# Revit family: AL_ST-STS1_приток
name_source: partatom
category: Воздухораспределители
revit_build: Autodesk Revit 2014 (Build: 20130308_1515(x64)
units: mm (PartAtom-declared; Revit-internal decimal feet)

## types (1242) — shared parameters
A = 23 мм
URL = http://inplast.ru
margins = 12 мм
Изготовитель = INPLAST-SMAY
Материал = Алюминий_RAL9016 (INPLAST)
Описание = Решетка AL-STS1 тип сетки - сетка просечно-вытяжная 4.5х9.0мм
Сетка = Сетка просечная[горизонтальная]_RAL9016 (INPLAST)

## per-type parameters (varying)
| type | Aef | C | C' | D | D' | Тип крепежа |
| AL-STS-1-100х100-АА | 0.006 м² | 100 мм | 95 мм | 100 мм | 95 мм | саморезы |
| AL-STS-1-125х100-АА | 0.008 м² | 125 мм | 120 мм | 100 мм | 95 мм | саморезы |
| AL-STS-1-125х125-АА | 0.009 м² | 125 мм | 120 мм | 125 мм | 120 мм | саморезы |
| AL-STS-1-150х100-АА | 0.009 м² | 150 мм | 145 мм | 100 мм | 95 мм | саморезы |
| AL-STS-1-150х125-АА | 0.011 м² | 150 мм | 145 мм | 125 мм | 120 мм | саморезы |
| AL-STS-1-150х150-АА | 0.014 м² | 150 мм | 145 мм | 150 мм | 145 мм | саморезы |
| AL-STS-1-200х100-АА | 0.012 м² | 200 мм | 195 мм | 100 мм | 95 мм | саморезы |
| AL-STS-1-200х125-АА | 0.015 м² | 200 мм | 195 мм | 125 мм | 120 мм | саморезы |
| AL-STS-1-200х150-АА | 0.018 м² | 200 мм | 195 мм | 150 мм | 145 мм | саморезы |
| AL-STS-1-200х200-АА | 0.024 м² | 200 мм | 195 мм | 200 мм | 195 мм | саморезы |
| AL-STS-1-225х100-АА | 0.014 м² | 225 мм | 220 мм | 100 мм | 95 мм | саморезы |
| AL-STS-1-225х125-АА | 0.017 м² | 225 мм | 220 мм | 125 мм | 120 мм | саморезы |
| AL-STS-1-225х150-АА | 0.020 м² | 225 мм | 220 мм | 150 мм | 145 мм | саморезы |
| AL-STS-1-225х200-АА | 0.027 м² | 225 мм | 220 мм | 200 мм | 195 мм | саморезы |
| AL-STS-1-225х225-АА | 0.030 м² | 225 мм | 220 мм | 225 мм | 220 мм | саморезы |
| AL-STS-1-250х100-АА | 0.015 м² | 250 мм | 245 мм | 100 мм | 95 мм | саморезы |
| AL-STS-1-250х125-АА | 0.019 м² | 250 мм | 245 мм | 125 мм | 120 мм | саморезы |
| AL-STS-1-250х150-АА | 0.023 м² | 250 мм | 245 мм | 150 мм | 145 мм | саморезы |
| AL-STS-1-250х200-АА | 0.030 м² | 250 мм | 245 мм | 200 мм | 195 мм | саморезы |
| AL-STS-1-250х225-АА | 0.034 м² | 250 мм | 245 мм | 225 мм | 220 мм | саморезы |
| AL-STS-1-250х250-АА | 0.038 м² | 250 мм | 245 мм | 250 мм | 245 мм | саморезы |
| AL-STS-1-300х100-АА | 0.018 м² | 300 мм | 295 мм | 100 мм | 95 мм | саморезы |
| AL-STS-1-300х125-АА | 0.023 м² | 300 мм | 295 мм | 125 мм | 120 мм | саморезы |
| AL-STS-1-300х150-АА | 0.027 м² | 300 мм | 295 мм | 150 мм | 145 мм | саморезы |
| AL-STS-1-300х200-АА | 0.036 м² | 300 мм | 295 мм | 200 мм | 195 мм | саморезы |
| AL-STS-1-300х225-АА | 0.041 м² | 300 мм | 295 мм | 225 мм | 220 мм | саморезы |
| AL-STS-1-300х250-АА | 0.045 м² | 300 мм | 295 мм | 250 мм | 245 мм | саморезы |
| AL-STS-1-300х300-АА | 0.054 м² | 300 мм | 295 мм | 300 мм | 295 мм | саморезы |
| AL-STS-1-325х100-АА | 0.020 м² | 325 мм | 320 мм | 100 мм | 95 мм | саморезы |
| AL-STS-1-325х125-АА | 0.024 м² | 325 мм | 320 мм | 125 мм | 120 мм | саморезы |
| AL-STS-1-325х150-АА | 0.029 м² | 325 мм | 320 мм | 150 мм | 145 мм | саморезы |
| AL-STS-1-325х200-АА | 0.039 м² | 325 мм | 320 мм | 200 мм | 195 мм | саморезы |
| AL-STS-1-325х225-АА | 0.044 м² | 325 мм | 320 мм | 225 мм | 220 мм | саморезы |
| AL-STS-1-325х250-АА | 0.049 м² | 325 мм | 320 мм | 250 мм | 245 мм | саморезы |
| AL-STS-1-325х300-АА | 0.059 м² | 325 мм | 320 мм | 300 мм | 295 мм | саморезы |
| AL-STS-1-325х325-АА | 0.064 м² | 325 мм | 320 мм | 325 мм | 320 мм | саморезы |
| AL-STS-1-350х100-АА | 0.021 м² | 350 мм | 345 мм | 100 мм | 95 мм | саморезы |
| AL-STS-1-350х125-АА | 0.026 м² | 350 мм | 345 мм | 125 мм | 120 мм | саморезы |
| AL-STS-1-350х150-АА | 0.032 м² | 350 мм | 345 мм | 150 мм | 145 мм | саморезы |
| AL-STS-1-350х200-АА | 0.042 м² | 350 мм | 345 мм | 200 мм | 195 мм | саморезы |
| AL-STS-1-350х225-АА | 0.047 м² | 350 мм | 345 мм | 225 мм | 220 мм | саморезы |
| AL-STS-1-350х250-АА | 0.053 м² | 350 мм | 345 мм | 250 мм | 245 мм | саморезы |
| AL-STS-1-350х300-АА | 0.063 м² | 350 мм | 345 мм | 300 мм | 295 мм | саморезы |
| AL-STS-1-350х325-АА | 0.068 м² | 350 мм | 345 мм | 325 мм | 320 мм | саморезы |
| AL-STS-1-350х350-АА | 0.074 м² | 350 мм | 345 мм | 350 мм | 345 мм | саморезы |
| AL-STS-1-400х100-АА | 0.024 м² | 400 мм | 395 мм | 100 мм | 95 мм | саморезы |
| AL-STS-1-400х125-АА | 0.030 м² | 400 мм | 395 мм | 125 мм | 120 мм | саморезы |
| AL-STS-1-400х150-АА | 0.036 м² | 400 мм | 395 мм | 150 мм | 145 мм | саморезы |
| AL-STS-1-400х200-АА | 0.048 м² | 400 мм | 395 мм | 200 мм | 195 мм | саморезы |
| AL-STS-1-400х225-АА | 0.054 м² | 400 мм | 395 мм | 225 мм | 220 мм | саморезы |
| AL-STS-1-400х250-АА | 0.060 м² | 400 мм | 395 мм | 250 мм | 245 мм | саморезы |
| AL-STS-1-400х300-АА | 0.072 м² | 400 мм | 395 мм | 300 мм | 295 мм | саморезы |
| AL-STS-1-400х325-АА | 0.078 м² | 400 мм | 395 мм | 325 мм | 320 мм | саморезы |
| AL-STS-1-400х350-АА | 0.084 м² | 400 мм | 395 мм | 350 мм | 345 мм | саморезы |
| AL-STS-1-400х400-АА | 0.096 м² | 400 мм | 395 мм | 400 мм | 395 мм | саморезы |
| AL-STS-1-425х100-АА | 0.026 м² | 425 мм | 420 мм | 100 мм | 95 мм | саморезы |
| AL-STS-1-425х125-АА | 0.032 м² | 425 мм | 420 мм | 125 мм | 120 мм | саморезы |
| AL-STS-1-425х150-АА | 0.038 м² | 425 мм | 420 мм | 150 мм | 145 мм | саморезы |
| AL-STS-1-425х200-АА | 0.051 м² | 425 мм | 420 мм | 200 мм | 195 мм | саморезы |
| AL-STS-1-425х225-АА | 0.058 м² | 425 мм | 420 мм | 225 мм | 220 мм | саморезы |
| AL-STS-1-425х250-АА | 0.064 м² | 425 мм | 420 мм | 250 мм | 245 мм | саморезы |
| AL-STS-1-425х300-АА | 0.077 м² | 425 мм | 420 мм | 300 мм | 295 мм | саморезы |
| AL-STS-1-425х325-АА | 0.083 м² | 425 мм | 420 мм | 325 мм | 320 мм | саморезы |
| AL-STS-1-425х350-АА | 0.089 м² | 425 мм | 420 мм | 350 мм | 345 мм | саморезы |
| AL-STS-1-425х400-АА | 0.102 м² | 425 мм | 420 мм | 400 мм | 395 мм | саморезы |
| AL-STS-1-425х425-АА | 0.109 м² | 425 мм | 420 мм | 425 мм | 420 мм | саморезы |
| AL-STS-1-450х100-АА | 0.027 м² | 450 мм | 445 мм | 100 мм | 95 мм | саморезы |
| AL-STS-1-450х125-АА | 0.034 м² | 450 мм | 445 мм | 125 мм | 120 мм | саморезы |
| AL-STS-1-450х150-АА | 0.041 м² | 450 мм | 445 мм | 150 мм | 145 мм | саморезы |
| AL-STS-1-450х200-АА | 0.054 м² | 450 мм | 445 мм | 200 мм | 195 мм | саморезы |
| AL-STS-1-450х225-АА | 0.061 м² | 450 мм | 445 мм | 225 мм | 220 мм | саморезы |
| AL-STS-1-450х250-АА | 0.068 м² | 450 мм | 445 мм | 250 мм | 245 мм | саморезы |
| AL-STS-1-450х300-АА | 0.081 м² | 450 мм | 445 мм | 300 мм | 295 мм | саморезы |
| AL-STS-1-450х325-АА | 0.088 м² | 450 мм | 445 мм | 325 мм | 320 мм | саморезы |
| AL-STS-1-450х350-АА | 0.095 м² | 450 мм | 445 мм | 350 мм | 345 мм | саморезы |
| AL-STS-1-450х400-АА | 0.108 м² | 450 мм | 445 мм | 400 мм | 395 мм | саморезы |
| AL-STS-1-450х425-АА | 0.115 м² | 450 мм | 445 мм | 425 мм | 420 мм | саморезы |
| AL-STS-1-450х450-АА | 0.122 м² | 450 мм | 445 мм | 450 мм | 445 мм | саморезы |
| AL-STS-1-500х100-АА | 0.030 м² | 500 мм | 495 мм | 100 мм | 95 мм | саморезы |
| AL-STS-1-500х125-АА | 0.038 м² | 500 мм | 495 мм | 125 мм | 120 мм | саморезы |
| AL-STS-1-500х150-АА | 0.045 м² | 500 мм | 495 мм | 150 мм | 145 мм | саморезы |
| AL-STS-1-500х200-АА | 0.060 м² | 500 мм | 495 мм | 200 мм | 195 мм | саморезы |
| AL-STS-1-500х225-АА | 0.068 м² | 500 мм | 495 мм | 225 мм | 220 мм | саморезы |
| AL-STS-1-500х250-АА | 0.075 м² | 500 мм | 495 мм | 250 мм | 245 мм | саморезы |
| AL-STS-1-500х300-АА | 0.090 м² | 500 мм | 495 мм | 300 мм | 295 мм | саморезы |
| AL-STS-1-500х325-АА | 0.098 м² | 500 мм | 495 мм | 325 мм | 320 мм | саморезы |
| AL-STS-1-500х350-АА | 0.105 м² | 500 мм | 495 мм | 350 мм | 345 мм | саморезы |
| AL-STS-1-500х400-АА | 0.120 м² | 500 мм | 495 мм | 400 мм | 395 мм | саморезы |
| AL-STS-1-500х425-АА | 0.128 м² | 500 мм | 495 мм | 425 мм | 420 мм | саморезы |
| AL-STS-1-500х450-АА | 0.135 м² | 500 мм | 495 мм | 450 мм | 445 мм | саморезы |
| AL-STS-1-500х500-АА | 0.150 м² | 500 мм | 495 мм | 500 мм | 495 мм | саморезы |
| AL-STS-1-525х100-АА | 0.032 м² | 525 мм | 520 мм | 100 мм | 95 мм | саморезы |
| AL-STS-1-525х125-АА | 0.039 м² | 525 мм | 520 мм | 125 мм | 120 мм | саморезы |
| AL-STS-1-525х150-АА | 0.047 м² | 525 мм | 520 мм | 150 мм | 145 мм | саморезы |
| AL-STS-1-525х200-АА | 0.063 м² | 525 мм | 520 мм | 200 мм | 195 мм | саморезы |
| AL-STS-1-525х225-АА | 0.071 м² | 525 мм | 520 мм | 225 мм | 220 мм | саморезы |
| AL-STS-1-525х250-АА | 0.079 м² | 525 мм | 520 мм | 250 мм | 245 мм | саморезы |
| AL-STS-1-525х300-АА | 0.095 м² | 525 мм | 520 мм | 300 мм | 295 мм | саморезы |
| AL-STS-1-525х325-АА | 0.103 м² | 525 мм | 520 мм | 325 мм | 320 мм | саморезы |
| AL-STS-1-525х350-АА | 0.111 м² | 525 мм | 520 мм | 350 мм | 345 мм | саморезы |
| AL-STS-1-525х400-АА | 0.126 м² | 525 мм | 520 мм | 400 мм | 395 мм | саморезы |
| AL-STS-1-525х425-АА | 0.134 м² | 525 мм | 520 мм | 425 мм | 420 мм | саморезы |
| AL-STS-1-525х450-АА | 0.142 м² | 525 мм | 520 мм | 450 мм | 445 мм | саморезы |
| AL-STS-1-525х500-АА | 0.158 м² | 525 мм | 520 мм | 500 мм | 495 мм | саморезы |
| AL-STS-1-525х525-АА | 0.166 м² | 525 мм | 520 мм | 525 мм | 520 мм | саморезы |
| AL-STS-1-550х100-АА | 0.033 м² | 550 мм | 545 мм | 100 мм | 95 мм | саморезы |
| AL-STS-1-550х125-АА | 0.041 м² | 550 мм | 545 мм | 125 мм | 120 мм | саморезы |
| AL-STS-1-550х150-АА | 0.050 м² | 550 мм | 545 мм | 150 мм | 145 мм | саморезы |
| AL-STS-1-550х200-АА | 0.066 м² | 550 мм | 545 мм | 200 мм | 195 мм | саморезы |
| AL-STS-1-550х225-АА | 0.074 м² | 550 мм | 545 мм | 225 мм | 220 мм | саморезы |
| AL-STS-1-550х250-АА | 0.083 м² | 550 мм | 545 мм | 250 мм | 245 мм | саморезы |
| AL-STS-1-550х300-АА | 0.099 м² | 550 мм | 545 мм | 300 мм | 295 мм | саморезы |
| AL-STS-1-550х325-АА | 0.108 м² | 550 мм | 545 мм | 325 мм | 320 мм | саморезы |
| AL-STS-1-550х350-АА | 0.116 м² | 550 мм | 545 мм | 350 мм | 345 мм | саморезы |
| AL-STS-1-550х400-АА | 0.132 м² | 550 мм | 545 мм | 400 мм | 395 мм | саморезы |
| AL-STS-1-550х425-АА | 0.141 м² | 550 мм | 545 мм | 425 мм | 420 мм | саморезы |
| AL-STS-1-550х450-АА | 0.149 м² | 550 мм | 545 мм | 450 мм | 445 мм | саморезы |
| AL-STS-1-550х500-АА | 0.165 м² | 550 мм | 545 мм | 500 мм | 495 мм | саморезы |
| AL-STS-1-550х525-АА | 0.174 м² | 550 мм | 545 мм | 525 мм | 520 мм | саморезы |
| AL-STS-1-550х550-АА | 0.182 м² | 550 мм | 545 мм | 550 мм | 545 мм | саморезы |
| AL-STS-1-600х100-АА | 0.036 м² | 600 мм | 595 мм | 100 мм | 95 мм | саморезы |
| AL-STS-1-600х125-АА | 0.045 м² | 600 мм | 595 мм | 125 мм | 120 мм | саморезы |
| AL-STS-1-600х150-АА | 0.054 м² | 600 мм | 595 мм | 150 мм | 145 мм | саморезы |
| AL-STS-1-600х200-АА | 0.072 м² | 600 мм | 595 мм | 200 мм | 195 мм | саморезы |
| AL-STS-1-600х225-АА | 0.081 м² | 600 мм | 595 мм | 225 мм | 220 мм | саморезы |
| AL-STS-1-600х250-АА | 0.090 м² | 600 мм | 595 мм | 250 мм | 245 мм | саморезы |
| AL-STS-1-600х300-АА | 0.108 м² | 600 мм | 595 мм | 300 мм | 295 мм | саморезы |
| AL-STS-1-600х325-АА | 0.117 м² | 600 мм | 595 мм | 325 мм | 320 мм | саморезы |
| AL-STS-1-600х350-АА | 0.126 м² | 600 мм | 595 мм | 350 мм | 345 мм | саморезы |
| AL-STS-1-600х400-АА | 0.144 м² | 600 мм | 595 мм | 400 мм | 395 мм | саморезы |
| AL-STS-1-600х425-АА | 0.153 м² | 600 мм | 595 мм | 425 мм | 420 мм | саморезы |
| AL-STS-1-600х450-АА | 0.162 м² | 600 мм | 595 мм | 450 мм | 445 мм | саморезы |
| AL-STS-1-600х500-АА | 0.180 м² | 600 мм | 595 мм | 500 мм | 495 мм | саморезы |
| AL-STS-1-600х525-АА | 0.190 м² | 600 мм | 595 мм | 525 мм | 520 мм | саморезы |
| AL-STS-1-600х550-АА | 0.199 м² | 600 мм | 595 мм | 550 мм | 545 мм | саморезы |
| AL-STS-1-600х600-АА | 0.217 м² | 600 мм | 595 мм | 600 мм | 595 мм | саморезы |
| AL-STS-1-625х100-АА | 0.038 м² | 625 мм | 620 мм | 100 мм | 95 мм | саморезы |
| AL-STS-1-625х125-АА | 0.047 м² | 625 мм | 620 мм | 125 мм | 120 мм | саморезы |
| AL-STS-1-625х150-АА | 0.056 м² | 625 мм | 620 мм | 150 мм | 145 мм | саморезы |
| AL-STS-1-625х200-АА | 0.075 м² | 625 мм | 620 мм | 200 мм | 195 мм | саморезы |
| AL-STS-1-625х225-АА | 0.085 м² | 625 мм | 620 мм | 225 мм | 220 мм | саморезы |
| AL-STS-1-625х250-АА | 0.094 м² | 625 мм | 620 мм | 250 мм | 245 мм | саморезы |
| AL-STS-1-625х300-АА | 0.113 м² | 625 мм | 620 мм | 300 мм | 295 мм | саморезы |
| AL-STS-1-625х325-АА | 0.122 м² | 625 мм | 620 мм | 325 мм | 320 мм | саморезы |
| AL-STS-1-625х350-АА | 0.132 м² | 625 мм | 620 мм | 350 мм | 345 мм | саморезы |
| AL-STS-1-625х400-АА | 0.150 м² | 625 мм | 620 мм | 400 мм | 395 мм | саморезы |
| AL-STS-1-625х425-АА | 0.160 м² | 625 мм | 620 мм | 425 мм | 420 мм | саморезы |
| AL-STS-1-625х450-АА | 0.169 м² | 625 мм | 620 мм | 450 мм | 445 мм | саморезы |
| AL-STS-1-625х500-АА | 0.188 м² | 625 мм | 620 мм | 500 мм | 495 мм | саморезы |
| AL-STS-1-625х525-АА | 0.197 м² | 625 мм | 620 мм | 525 мм | 520 мм | саморезы |
| AL-STS-1-625х550-АА | 0.207 м² | 625 мм | 620 мм | 550 мм | 545 мм | саморезы |
| AL-STS-1-625х600-АА | 0.226 м² | 625 мм | 620 мм | 600 мм | 595 мм | саморезы |
| AL-STS-1-625х625-АА | 0.235 м² | 625 мм | 620 мм | 625 мм | 620 мм | саморезы |
| AL-STS-1-650х100-АА | 0.039 м² | 650 мм | 645 мм | 100 мм | 95 мм | саморезы |
| AL-STS-1-650х125-АА | 0.049 м² | 650 мм | 645 мм | 125 мм | 120 мм | саморезы |
| AL-STS-1-650х150-АА | 0.059 м² | 650 мм | 645 мм | 150 мм | 145 мм | саморезы |
| AL-STS-1-650х200-АА | 0.078 м² | 650 мм | 645 мм | 200 мм | 195 мм | саморезы |
| AL-STS-1-650х225-АА | 0.088 м² | 650 мм | 645 мм | 225 мм | 220 мм | саморезы |
| AL-STS-1-650х250-АА | 0.098 м² | 650 мм | 645 мм | 250 мм | 245 мм | саморезы |
| AL-STS-1-650х300-АА | 0.117 м² | 650 мм | 645 мм | 300 мм | 295 мм | саморезы |
| AL-STS-1-650х325-АА | 0.127 м² | 650 мм | 645 мм | 325 мм | 320 мм | саморезы |
| AL-STS-1-650х350-АА | 0.137 м² | 650 мм | 645 мм | 350 мм | 345 мм | саморезы |
| AL-STS-1-650х400-АА | 0.156 м² | 650 мм | 645 мм | 400 мм | 395 мм | саморезы |
| AL-STS-1-650х425-АА | 0.166 м² | 650 мм | 645 мм | 425 мм | 420 мм | саморезы |
| AL-STS-1-650х450-АА | 0.176 м² | 650 мм | 645 мм | 450 мм | 445 мм | саморезы |
| AL-STS-1-650х500-АА | 0.196 м² | 650 мм | 645 мм | 500 мм | 495 мм | саморезы |
| AL-STS-1-650х525-АА | 0.205 м² | 650 мм | 645 мм | 525 мм | 520 мм | саморезы |
| AL-STS-1-650х550-АА | 0.215 м² | 650 мм | 645 мм | 550 мм | 545 мм | саморезы |
| AL-STS-1-650х600-АА | 0.235 м² | 650 мм | 645 мм | 600 мм | 595 мм | саморезы |
| AL-STS-1-650х625-АА | 0.244 м² | 650 мм | 645 мм | 625 мм | 620 мм | саморезы |
| AL-STS-1-650х650-АА | 0.254 м² | 650 мм | 645 мм | 650 мм | 645 мм | саморезы |
| AL-STS-1-700х100-АА | 0.042 м² | 700 мм | 695 мм | 100 мм | 95 мм | саморезы |
| AL-STS-1-700х125-АА | 0.053 м² | 700 мм | 695 мм | 125 мм | 120 мм | саморезы |
| AL-STS-1-700х150-АА | 0.063 м² | 700 мм | 695 мм | 150 мм | 145 мм | саморезы |
| AL-STS-1-700х200-АА | 0.084 м² | 700 мм | 695 мм | 200 мм | 195 мм | саморезы |
| AL-STS-1-700х225-АА | 0.095 м² | 700 мм | 695 мм | 225 мм | 220 мм | саморезы |
| AL-STS-1-700х250-АА | 0.105 м² | 700 мм | 695 мм | 250 мм | 245 мм | саморезы |
| AL-STS-1-700х300-АА | 0.126 м² | 700 мм | 695 мм | 300 мм | 295 мм | саморезы |
| AL-STS-1-700х325-АА | 0.137 м² | 700 мм | 695 мм | 325 мм | 320 мм | саморезы |
| AL-STS-1-700х350-АА | 0.147 м² | 700 мм | 695 мм | 350 мм | 345 мм | саморезы |
| AL-STS-1-700х400-АА | 0.168 м² | 700 мм | 695 мм | 400 мм | 395 мм | саморезы |
| AL-STS-1-700х425-АА | 0.179 м² | 700 мм | 695 мм | 425 мм | 420 мм | саморезы |
| AL-STS-1-700х450-АА | 0.190 м² | 700 мм | 695 мм | 450 мм | 445 мм | саморезы |
| AL-STS-1-700х500-АА | 0.211 м² | 700 мм | 695 мм | 500 мм | 495 мм | саморезы |
| AL-STS-1-700х525-АА | 0.221 м² | 700 мм | 695 мм | 525 мм | 520 мм | саморезы |
| AL-STS-1-700х550-АА | 0.232 м² | 700 мм | 695 мм | 550 мм | 545 мм | саморезы |
| AL-STS-1-700х600-АА | 0.253 м² | 700 мм | 695 мм | 600 мм | 595 мм | саморезы |
| AL-STS-1-700х625-АА | 0.263 м² | 700 мм | 695 мм | 625 мм | 620 мм | саморезы |
| AL-STS-1-700х650-АА | 0.274 м² | 700 мм | 695 мм | 650 мм | 645 мм | саморезы |
| AL-STS-1-725х100-АА | 0.044 м² | 725 мм | 720 мм | 100 мм | 95 мм | саморезы |
| AL-STS-1-725х125-АА | 0.055 м² | 725 мм | 720 мм | 125 мм | 120 мм | саморезы |
| AL-STS-1-725х150-АА | 0.065 м² | 725 мм | 720 мм | 150 мм | 145 мм | саморезы |
| AL-STS-1-725х200-АА | 0.087 м² | 725 мм | 720 мм | 200 мм | 195 мм | саморезы |
| AL-STS-1-725х225-АА | 0.098 м² | 725 мм | 720 мм | 225 мм | 220 мм | саморезы |
| AL-STS-1-725х250-АА | 0.109 м² | 725 мм | 720 мм | 250 мм | 245 мм | саморезы |
| AL-STS-1-725х300-АА | 0.131 м² | 725 мм | 720 мм | 300 мм | 295 мм | саморезы |
| AL-STS-1-725х325-АА | 0.142 м² | 725 мм | 720 мм | 325 мм | 320 мм | саморезы |
| AL-STS-1-725х350-АА | 0.153 м² | 725 мм | 720 мм | 350 мм | 345 мм | саморезы |
| AL-STS-1-725х400-АА | 0.174 м² | 725 мм | 720 мм | 400 мм | 395 мм | саморезы |
| AL-STS-1-725х425-АА | 0.185 м² | 725 мм | 720 мм | 425 мм | 420 мм | саморезы |
| AL-STS-1-725х450-АА | 0.196 м² | 725 мм | 720 мм | 450 мм | 445 мм | саморезы |
| AL-STS-1-725х500-АА | 0.218 м² | 725 мм | 720 мм | 500 мм | 495 мм | саморезы |
| AL-STS-1-725х525-АА | 0.229 м² | 725 мм | 720 мм | 525 мм | 520 мм | саморезы |
| AL-STS-1-725х550-АА | 0.240 м² | 725 мм | 720 мм | 550 мм | 545 мм | саморезы |
| AL-STS-1-725х600-АА | 0.262 м² | 725 мм | 720 мм | 600 мм | 595 мм | саморезы |
| AL-STS-1-725х625-АА | 0.273 м² | 725 мм | 720 мм | 625 мм | 620 мм | саморезы |
| AL-STS-1-725х650-АА | 0.284 м² | 725 мм | 720 мм | 650 мм | 645 мм | саморезы |
| AL-STS-1-750х100-АА | 0.045 м² | 750 мм | 745 мм | 100 мм | 95 мм | саморезы |
| AL-STS-1-750х125-АА | 0.056 м² | 750 мм | 745 мм | 125 мм | 120 мм | саморезы |
| AL-STS-1-750х150-АА | 0.068 м² | 750 мм | 745 мм | 150 мм | 145 мм | саморезы |
| AL-STS-1-750х200-АА | 0.090 м² | 750 мм | 745 мм | 200 мм | 195 мм | саморезы |
| AL-STS-1-750х225-АА | 0.102 м² | 750 мм | 745 мм | 225 мм | 220 мм | саморезы |
| AL-STS-1-750х250-АА | 0.113 м² | 750 мм | 745 мм | 250 мм | 245 мм | саморезы |
| AL-STS-1-750х300-АА | 0.135 м² | 750 мм | 745 мм | 300 мм | 295 мм | саморезы |
| AL-STS-1-750х325-АА | 0.147 м² | 750 мм | 745 мм | 325 мм | 320 мм | саморезы |
| AL-STS-1-750х350-АА | 0.158 м² | 750 мм | 745 мм | 350 мм | 345 мм | саморезы |
| AL-STS-1-750х400-АА | 0.180 м² | 750 мм | 745 мм | 400 мм | 395 мм | саморезы |
| AL-STS-1-750х425-АА | 0.192 м² | 750 мм | 745 мм | 425 мм | 420 мм | саморезы |
| AL-STS-1-750х450-АА | 0.203 м² | 750 мм | 745 мм | 450 мм | 445 мм | саморезы |
| AL-STS-1-750х500-АА | 0.226 м² | 750 мм | 745 мм | 500 мм | 495 мм | саморезы |
| AL-STS-1-750х525-АА | 0.237 м² | 750 мм | 745 мм | 525 мм | 520 мм | саморезы |
| AL-STS-1-750х550-АА | 0.248 м² | 750 мм | 745 мм | 550 мм | 545 мм | саморезы |
| AL-STS-1-750х600-АА | 0.271 м² | 750 мм | 745 мм | 600 мм | 595 мм | саморезы |
| AL-STS-1-750х625-АА | 0.282 м² | 750 мм | 745 мм | 625 мм | 620 мм | саморезы |
| AL-STS-1-750х650-АА | 0.293 м² | 750 мм | 745 мм | 650 мм | 645 мм | саморезы |
| AL-STS-1-800х100-АА | 0.048 м² | 800 мм | 795 мм | 100 мм | 95 мм | саморезы |
| AL-STS-1-800х125-АА | 0.060 м² | 800 мм | 795 мм | 125 мм | 120 мм | саморезы |
| AL-STS-1-800х150-АА | 0.072 м² | 800 мм | 795 мм | 150 мм | 145 мм | саморезы |
| AL-STS-1-800х200-АА | 0.096 м² | 800 мм | 795 мм | 200 мм | 195 мм | саморезы |
| AL-STS-1-800х225-АА | 0.108 м² | 800 мм | 795 мм | 225 мм | 220 мм | саморезы |
| AL-STS-1-800х250-АА | 0.120 м² | 800 мм | 795 мм | 250 мм | 245 мм | саморезы |
| AL-STS-1-800х300-АА | 0.144 м² | 800 мм | 795 мм | 300 мм | 295 мм | саморезы |
| AL-STS-1-800х325-АА | 0.156 м² | 800 мм | 795 мм | 325 мм | 320 мм | саморезы |
| AL-STS-1-800х350-АА | 0.168 м² | 800 мм | 795 мм | 350 мм | 345 мм | саморезы |
| AL-STS-1-800х400-АА | 0.193 м² | 800 мм | 795 мм | 400 мм | 395 мм | саморезы |
| AL-STS-1-800х425-АА | 0.205 м² | 800 мм | 795 мм | 425 мм | 420 мм | саморезы |
| AL-STS-1-800х450-АА | 0.217 м² | 800 мм | 795 мм | 450 мм | 445 мм | саморезы |
| AL-STS-1-800х500-АА | 0.241 м² | 800 мм | 795 мм | 500 мм | 495 мм | саморезы |
| AL-STS-1-800х525-АА | 0.253 м² | 800 мм | 795 мм | 525 мм | 520 мм | саморезы |
| AL-STS-1-800х550-АА | 0.265 м² | 800 мм | 795 мм | 550 мм | 545 мм | саморезы |
| AL-STS-1-800х600-АА | 0.289 м² | 800 мм | 795 мм | 600 мм | 595 мм | саморезы |
| AL-STS-1-800х625-АА | 0.301 м² | 800 мм | 795 мм | 625 мм | 620 мм | саморезы |
| AL-STS-1-800х650-АА | 0.313 м² | 800 мм | 795 мм | 650 мм | 645 мм | саморезы |
| AL-STS-1-825х100-АА | 0.050 м² | 825 мм | 820 мм | 100 мм | 95 мм | саморезы |
| AL-STS-1-825х125-АА | 0.062 м² | 825 мм | 820 мм | 125 мм | 120 мм | саморезы |
| AL-STS-1-825х150-АА | 0.074 м² | 825 мм | 820 мм | 150 мм | 145 мм | саморезы |
| AL-STS-1-825х200-АА | 0.099 м² | 825 мм | 820 мм | 200 мм | 195 мм | саморезы |
| AL-STS-1-825х225-АА | 0.112 м² | 825 мм | 820 мм | 225 мм | 220 мм | саморезы |
| AL-STS-1-825х250-АА | 0.124 м² | 825 мм | 820 мм | 250 мм | 245 мм | саморезы |
| AL-STS-1-825х300-АА | 0.149 м² | 825 мм | 820 мм | 300 мм | 295 мм | саморезы |
| AL-STS-1-825х325-АА | 0.161 м² | 825 мм | 820 мм | 325 мм | 320 мм | саморезы |
| AL-STS-1-825х350-АА | 0.174 м² | 825 мм | 820 мм | 350 мм | 345 мм | саморезы |
| AL-STS-1-825х400-АА | 0.199 м² | 825 мм | 820 мм | 400 мм | 395 мм | саморезы |
| AL-STS-1-825х425-АА | 0.211 м² | 825 мм | 820 мм | 425 мм | 420 мм | саморезы |
| AL-STS-1-825х450-АА | 0.223 м² | 825 мм | 820 мм | 450 мм | 445 мм | саморезы |
| AL-STS-1-825х500-АА | 0.248 м² | 825 мм | 820 мм | 500 мм | 495 мм | саморезы |
| AL-STS-1-825х525-АА | 0.261 м² | 825 мм | 820 мм | 525 мм | 520 мм | саморезы |
| AL-STS-1-825х550-АА | 0.273 м² | 825 мм | 820 мм | 550 мм | 545 мм | саморезы |
| AL-STS-1-825х600-АА | 0.298 м² | 825 мм | 820 мм | 600 мм | 595 мм | саморезы |
| AL-STS-1-825х625-АА | 0.310 м² | 825 мм | 820 мм | 625 мм | 620 мм | саморезы |
| AL-STS-1-825х650-АА | 0.323 м² | 825 мм | 820 мм | 650 мм | 645 мм | саморезы |
| AL-STS-1-850х100-АА | 0.051 м² | 850 мм | 845 мм | 100 мм | 95 мм | саморезы |
| AL-STS-1-850х125-АА | 0.064 м² | 850 мм | 845 мм | 125 мм | 120 мм | саморезы |
| AL-STS-1-850х150-АА | 0.077 м² | 850 мм | 845 мм | 150 мм | 145 мм | саморезы |
| AL-STS-1-850х200-АА | 0.102 м² | 850 мм | 845 мм | 200 мм | 195 мм | саморезы |
| AL-STS-1-850х225-АА | 0.115 м² | 850 мм | 845 мм | 225 мм | 220 мм | саморезы |
| AL-STS-1-850х250-АА | 0.128 м² | 850 мм | 845 мм | 250 мм | 245 мм | саморезы |
| AL-STS-1-850х300-АА | 0.153 м² | 850 мм | 845 мм | 300 мм | 295 мм | саморезы |
| AL-STS-1-850х325-АА | 0.166 м² | 850 мм | 845 мм | 325 мм | 320 мм | саморезы |
| AL-STS-1-850х350-АА | 0.179 м² | 850 мм | 845 мм | 350 мм | 345 мм | саморезы |
| AL-STS-1-850х400-АА | 0.205 м² | 850 мм | 845 мм | 400 мм | 395 мм | саморезы |
| AL-STS-1-850х425-АА | 0.217 м² | 850 мм | 845 мм | 425 мм | 420 мм | саморезы |
| AL-STS-1-850х450-АА | 0.230 м² | 850 мм | 845 мм | 450 мм | 445 мм | саморезы |
| AL-STS-1-850х500-АА | 0.256 м² | 850 мм | 845 мм | 500 мм | 495 мм | саморезы |
| AL-STS-1-850х525-АА | 0.268 м² | 850 мм | 845 мм | 525 мм | 520 мм | саморезы |
| AL-STS-1-850х550-АА | 0.281 м² | 850 мм | 845 мм | 550 мм | 545 мм | саморезы |
| AL-STS-1-850х600-АА | 0.307 м² | 850 мм | 845 мм | 600 мм | 595 мм | саморезы |
| AL-STS-1-850х625-АА | 0.320 м² | 850 мм | 845 мм | 625 мм | 620 мм | саморезы |
| AL-STS-1-850х650-АА | 0.332 м² | 850 мм | 845 мм | 650 мм | 645 мм | саморезы |
| AL-STS-1-900х100-АА | 0.054 м² | 900 мм | 895 мм | 100 мм | 95 мм | саморезы |
| AL-STS-1-900х125-АА | 0.068 м² | 900 мм | 895 мм | 125 мм | 120 мм | саморезы |
| AL-STS-1-900х150-АА | 0.081 м² | 900 мм | 895 мм | 150 мм | 145 мм | саморезы |
| AL-STS-1-900х200-АА | 0.108 м² | 900 мм | 895 мм | 200 мм | 195 мм | саморезы |
| AL-STS-1-900х225-АА | 0.122 м² | 900 мм | 895 мм | 225 мм | 220 мм | саморезы |
| AL-STS-1-900х250-АА | 0.135 м² | 900 мм | 895 мм | 250 мм | 245 мм | саморезы |
| AL-STS-1-900х300-АА | 0.162 м² | 900 мм | 895 мм | 300 мм | 295 мм | саморезы |
| AL-STS-1-900х325-АА | 0.176 м² | 900 мм | 895 мм | 325 мм | 320 мм | саморезы |
| AL-STS-1-900х350-АА | 0.190 м² | 900 мм | 895 мм | 350 мм | 345 мм | саморезы |
| AL-STS-1-900х400-АА | 0.217 м² | 900 мм | 895 мм | 400 мм | 395 мм | саморезы |
| AL-STS-1-900х425-АА | 0.230 м² | 900 мм | 895 мм | 425 мм | 420 мм | саморезы |
| AL-STS-1-900х450-АА | 0.244 м² | 900 мм | 895 мм | 450 мм | 445 мм | саморезы |
| AL-STS-1-900х500-АА | 0.271 м² | 900 мм | 895 мм | 500 мм | 495 мм | саморезы |
| AL-STS-1-900х525-АА | 0.284 м² | 900 мм | 895 мм | 525 мм | 520 мм | саморезы |
| AL-STS-1-900х550-АА | 0.298 м² | 900 мм | 895 мм | 550 мм | 545 мм | саморезы |
| AL-STS-1-900х600-АА | 0.325 м² | 900 мм | 895 мм | 600 мм | 595 мм | саморезы |
| AL-STS-1-900х625-АА | 0.338 м² | 900 мм | 895 мм | 625 мм | 620 мм | саморезы |
| AL-STS-1-900х650-АА | 0.352 м² | 900 мм | 895 мм | 650 мм | 645 мм | саморезы |
| AL-STS-1-925х100-АА | 0.056 м² | 925 мм | 920 мм | 100 мм | 95 мм | саморезы |
| AL-STS-1-925х125-АА | 0.070 м² | 925 мм | 920 мм | 125 мм | 120 мм | саморезы |
| AL-STS-1-925х150-АА | 0.083 м² | 925 мм | 920 мм | 150 мм | 145 мм | саморезы |
| AL-STS-1-925х200-АА | 0.111 м² | 925 мм | 920 мм | 200 мм | 195 мм | саморезы |
| AL-STS-1-925х225-АА | 0.125 м² | 925 мм | 920 мм | 225 мм | 220 мм | саморезы |
| AL-STS-1-925х250-АА | 0.139 м² | 925 мм | 920 мм | 250 мм | 245 мм | саморезы |
| AL-STS-1-925х300-АА | 0.167 м² | 925 мм | 920 мм | 300 мм | 295 мм | саморезы |
| AL-STS-1-925х325-АА | 0.181 м² | 925 мм | 920 мм | 325 мм | 320 мм | саморезы |
| AL-STS-1-925х350-АА | 0.195 м² | 925 мм | 920 мм | 350 мм | 345 мм | саморезы |
| AL-STS-1-925х400-АА | 0.223 м² | 925 мм | 920 мм | 400 мм | 395 мм | саморезы |
| AL-STS-1-925х425-АА | 0.237 м² | 925 мм | 920 мм | 425 мм | 420 мм | саморезы |
| AL-STS-1-925х450-АА | 0.250 м² | 925 мм | 920 мм | 450 мм | 445 мм | саморезы |
| AL-STS-1-925х500-АА | 0.278 м² | 925 мм | 920 мм | 500 мм | 495 мм | саморезы |
| AL-STS-1-925х525-АА | 0.292 м² | 925 мм | 920 мм | 525 мм | 520 мм | саморезы |
| AL-STS-1-925х550-АА | 0.306 м² | 925 мм | 920 мм | 550 мм | 545 мм | саморезы |
| AL-STS-1-925х600-АА | 0.334 м² | 925 мм | 920 мм | 600 мм | 595 мм | саморезы |
| AL-STS-1-925х625-АА | 0.348 м² | 925 мм | 920 мм | 625 мм | 620 мм | саморезы |
| AL-STS-1-925х650-АА | 0.362 м² | 925 мм | 920 мм | 650 мм | 645 мм | саморезы |
| AL-STS-1-950х100-АА | 0.057 м² | 950 мм | 945 мм | 100 мм | 95 мм | саморезы |
| AL-STS-1-950х125-АА | 0.071 м² | 950 мм | 945 мм | 125 мм | 120 мм | саморезы |
| AL-STS-1-950х150-АА | 0.086 м² | 950 мм | 945 мм | 150 мм | 145 мм | саморезы |
| AL-STS-1-950х200-АА | 0.114 м² | 950 мм | 945 мм | 200 мм | 195 мм | саморезы |
| AL-STS-1-950х225-АА | 0.129 м² | 950 мм | 945 мм | 225 мм | 220 мм | саморезы |
| AL-STS-1-950х250-АА | 0.143 м² | 950 мм | 945 мм | 250 мм | 245 мм | саморезы |
| AL-STS-1-950х300-АА | 0.171 м² | 950 мм | 945 мм | 300 мм | 295 мм | саморезы |
| AL-STS-1-950х325-АА | 0.186 м² | 950 мм | 945 мм | 325 мм | 320 мм | саморезы |
| AL-STS-1-950х350-АА | 0.200 м² | 950 мм | 945 мм | 350 мм | 345 мм | саморезы |
| AL-STS-1-950х400-АА | 0.229 м² | 950 мм | 945 мм | 400 мм | 395 мм | саморезы |
| AL-STS-1-950х425-АА | 0.243 м² | 950 мм | 945 мм | 425 мм | 420 мм | саморезы |
| AL-STS-1-950х450-АА | 0.257 м² | 950 мм | 945 мм | 450 мм | 445 мм | саморезы |
| AL-STS-1-950х500-АА | 0.286 м² | 950 мм | 945 мм | 500 мм | 495 мм | саморезы |
| AL-STS-1-950х525-АА | 0.300 м² | 950 мм | 945 мм | 525 мм | 520 мм | саморезы |
| AL-STS-1-950х550-АА | 0.314 м² | 950 мм | 945 мм | 550 мм | 545 мм | саморезы |
| AL-STS-1-950х600-АА | 0.343 м² | 950 мм | 945 мм | 600 мм | 595 мм | саморезы |
| AL-STS-1-950х625-АА | 0.357 м² | 950 мм | 945 мм | 625 мм | 620 мм | саморезы |
| AL-STS-1-950х650-АА | 0.371 м² | 950 мм | 945 мм | 650 мм | 645 мм | саморезы |
| AL-STS-1-1000х100-АА | 0.060 м² | 1000 мм | 995 мм | 100 мм | 95 мм | саморезы |
| AL-STS-1-1000х125-АА | 0.075 м² | 1000 мм | 995 мм | 125 мм | 120 мм | саморезы |
| AL-STS-1-1000х150-АА | 0.090 м² | 1000 мм | 995 мм | 150 мм | 145 мм | саморезы |
| AL-STS-1-1000х200-АА | 0.120 м² | 1000 мм | 995 мм | 200 мм | 195 мм | саморезы |
| AL-STS-1-1000х225-АА | 0.135 м² | 1000 мм | 995 мм | 225 мм | 220 мм | саморезы |
| AL-STS-1-1000х250-АА | 0.150 м² | 1000 мм | 995 мм | 250 мм | 245 мм | саморезы |
| AL-STS-1-1000х300-АА | 0.180 м² | 1000 мм | 995 мм | 300 мм | 295 мм | саморезы |
| AL-STS-1-1000х325-АА | 0.196 м² | 1000 мм | 995 мм | 325 мм | 320 мм | саморезы |
| AL-STS-1-1000х350-АА | 0.211 м² | 1000 мм | 995 мм | 350 мм | 345 мм | саморезы |
| AL-STS-1-1000х400-АА | 0.241 м² | 1000 мм | 995 мм | 400 мм | 395 мм | саморезы |
| AL-STS-1-1000х425-АА | 0.256 м² | 1000 мм | 995 мм | 425 мм | 420 мм | саморезы |
| AL-STS-1-1000х450-АА | 0.271 м² | 1000 мм | 995 мм | 450 мм | 445 мм | саморезы |
| AL-STS-1-1000х500-АА | 0.301 м² | 1000 мм | 995 мм | 500 мм | 495 мм | саморезы |
| AL-STS-1-1000х525-АА | 0.316 м² | 1000 мм | 995 мм | 525 мм | 520 мм | саморезы |
| AL-STS-1-1000х550-АА | 0.331 м² | 1000 мм | 995 мм | 550 мм | 545 мм | саморезы |
| AL-STS-1-1000х600-АА | 0.361 м² | 1000 мм | 995 мм | 600 мм | 595 мм | саморезы |
| AL-STS-1-1000х625-АА | 0.376 м² | 1000 мм | 995 мм | 625 мм | 620 мм | саморезы |
| AL-STS-1-1000х650-АА | 0.391 м² | 1000 мм | 995 мм | 650 мм | 645 мм | саморезы |
| AL-STS-1-1025х100-АА | 0.062 м² | 1025 мм | 1020 мм | 100 мм | 95 мм | саморезы |
| AL-STS-1-1025х125-АА | 0.077 м² | 1025 мм | 1020 мм | 125 мм | 120 мм | саморезы |
| AL-STS-1-1025х150-АА | 0.092 м² | 1025 мм | 1020 мм | 150 мм | 145 мм | саморезы |
| AL-STS-1-1025х200-АА | 0.123 м² | 1025 мм | 1020 мм | 200 мм | 195 мм | саморезы |
| AL-STS-1-1025х225-АА | 0.139 м² | 1025 мм | 1020 мм | 225 мм | 220 мм | саморезы |
| AL-STS-1-1025х250-АА | 0.154 м² | 1025 мм | 1020 мм | 250 мм | 245 мм | саморезы |
| AL-STS-1-1025х300-АА | 0.185 м² | 1025 мм | 1020 мм | 300 мм | 295 мм | саморезы |
| AL-STS-1-1025х325-АА | 0.200 м² | 1025 мм | 1020 мм | 325 мм | 320 мм | саморезы |
| AL-STS-1-1025х350-АА | 0.216 м² | 1025 мм | 1020 мм | 350 мм | 345 мм | саморезы |
| AL-STS-1-1025х400-АА | 0.247 м² | 1025 мм | 1020 мм | 400 мм | 395 мм | саморезы |
| AL-STS-1-1025х425-АА | 0.262 м² | 1025 мм | 1020 мм | 425 мм | 420 мм | саморезы |
| AL-STS-1-1025х450-АА | 0.277 м² | 1025 мм | 1020 мм | 450 мм | 445 мм | саморезы |
| AL-STS-1-1025х500-АА | 0.308 м² | 1025 мм | 1020 мм | 500 мм | 495 мм | саморезы |
| AL-STS-1-1025х525-АА | 0.324 м² | 1025 мм | 1020 мм | 525 мм | 520 мм | саморезы |
| AL-STS-1-1025х550-АА | 0.339 м² | 1025 мм | 1020 мм | 550 мм | 545 мм | саморезы |
| AL-STS-1-1025х600-АА | 0.370 м² | 1025 мм | 1020 мм | 600 мм | 595 мм | саморезы |
| AL-STS-1-1025х625-АА | 0.385 м² | 1025 мм | 1020 мм | 625 мм | 620 мм | саморезы |
| AL-STS-1-1025х650-АА | 0.401 м² | 1025 мм | 1020 мм | 650 мм | 645 мм | саморезы |
| AL-STS-1-1050х100-АА | 0.063 м² | 1050 мм | 1045 мм | 100 мм | 95 мм | саморезы |
| AL-STS-1-1050х125-АА | 0.079 м² | 1050 мм | 1045 мм | 125 мм | 120 мм | саморезы |
| AL-STS-1-1050х150-АА | 0.095 м² | 1050 мм | 1045 мм | 150 мм | 145 мм | саморезы |
| AL-STS-1-1050х200-АА | 0.126 м² | 1050 мм | 1045 мм | 200 мм | 195 мм | саморезы |
| AL-STS-1-1050х225-АА | 0.142 м² | 1050 мм | 1045 мм | 225 мм | 220 мм | саморезы |
| AL-STS-1-1050х250-АА | 0.158 м² | 1050 мм | 1045 мм | 250 мм | 245 мм | саморезы |
| AL-STS-1-1050х300-АА | 0.190 м² | 1050 мм | 1045 мм | 300 мм | 295 мм | саморезы |
| AL-STS-1-1050х325-АА | 0.205 м² | 1050 мм | 1045 мм | 325 мм | 320 мм | саморезы |
| AL-STS-1-1050х350-АА | 0.221 м² | 1050 мм | 1045 мм | 350 мм | 345 мм | саморезы |
| AL-STS-1-1050х400-АА | 0.253 м² | 1050 мм | 1045 мм | 400 мм | 395 мм | саморезы |
| AL-STS-1-1050х425-АА | 0.268 м² | 1050 мм | 1045 мм | 425 мм | 420 мм | саморезы |
| AL-STS-1-1050х450-АА | 0.284 м² | 1050 мм | 1045 мм | 450 мм | 445 мм | саморезы |
| AL-STS-1-1050х500-АА | 0.316 м² | 1050 мм | 1045 мм | 500 мм | 495 мм | саморезы |
| AL-STS-1-1050х525-АА | 0.332 м² | 1050 мм | 1045 мм | 525 мм | 520 мм | саморезы |
| AL-STS-1-1050х550-АА | 0.347 м² | 1050 мм | 1045 мм | 550 мм | 545 мм | саморезы |
| AL-STS-1-1050х600-АА | 0.379 м² | 1050 мм | 1045 мм | 600 мм | 595 мм | саморезы |
| AL-STS-1-1050х625-АА | 0.395 м² | 1050 мм | 1045 мм | 625 мм | 620 мм | саморезы |
| AL-STS-1-1050х650-АА | 0.411 м² | 1050 мм | 1045 мм | 650 мм | 645 мм | саморезы |
| AL-STS-1-1100х100-АА | 0.066 м² | 1100 мм | 1095 мм | 100 мм | 95 мм | саморезы |
| AL-STS-1-1100х125-АА | 0.083 м² | 1100 мм | 1095 мм | 125 мм | 120 мм | саморезы |
| AL-STS-1-1100х150-АА | 0.099 м² | 1100 мм | 1095 мм | 150 мм | 145 мм | саморезы |
| AL-STS-1-1100х200-АА | 0.132 м² | 1100 мм | 1095 мм | 200 мм | 195 мм | саморезы |
| AL-STS-1-1100х225-АА | 0.149 м² | 1100 мм | 1095 мм | 225 мм | 220 мм | саморезы |
| AL-STS-1-1100х250-АА | 0.165 м² | 1100 мм | 1095 мм | 250 мм | 245 мм | саморезы |
| AL-STS-1-1100х300-АА | 0.199 м² | 1100 мм | 1095 мм | 300 мм | 295 мм | саморезы |
| AL-STS-1-1100х325-АА | 0.215 м² | 1100 мм | 1095 мм | 325 мм | 320 мм | саморезы |
| AL-STS-1-1100х350-АА | 0.232 м² | 1100 мм | 1095 мм | 350 мм | 345 мм | саморезы |
| AL-STS-1-1100х400-АА | 0.265 м² | 1100 мм | 1095 мм | 400 мм | 395 мм | саморезы |
| AL-STS-1-1100х425-АА | 0.281 м² | 1100 мм | 1095 мм | 425 мм | 420 мм | саморезы |
| AL-STS-1-1100х450-АА | 0.298 м² | 1100 мм | 1095 мм | 450 мм | 445 мм | саморезы |
| AL-STS-1-1100х500-АА | 0.331 м² | 1100 мм | 1095 мм | 500 мм | 495 мм | саморезы |
| AL-STS-1-1100х525-АА | 0.347 м² | 1100 мм | 1095 мм | 525 мм | 520 мм | саморезы |
| AL-STS-1-1100х550-АА | 0.364 м² | 1100 мм | 1095 мм | 550 мм | 545 мм | саморезы |
| AL-STS-1-1100х600-АА | 0.397 м² | 1100 мм | 1095 мм | 600 мм | 595 мм | саморезы |
| AL-STS-1-1100х625-АА | 0.414 м² | 1100 мм | 1095 мм | 625 мм | 620 мм | саморезы |
| AL-STS-1-1100х650-АА | 0.430 м² | 1100 мм | 1095 мм | 650 мм | 645 мм | саморезы |
| AL-STS-1-1125х100-АА | 0.068 м² | 1125 мм | 1120 мм | 100 мм | 95 мм | саморезы |
| AL-STS-1-1125х125-АА | 0.085 м² | 1125 мм | 1120 мм | 125 мм | 120 мм | саморезы |
| AL-STS-1-1125х150-АА | 0.102 м² | 1125 мм | 1120 мм | 150 мм | 145 мм | саморезы |
| AL-STS-1-1125х200-АА | 0.135 м² | 1125 мм | 1120 мм | 200 мм | 195 мм | саморезы |
| AL-STS-1-1125х225-АА | 0.152 м² | 1125 мм | 1120 мм | 225 мм | 220 мм | саморезы |
| AL-STS-1-1125х250-АА | 0.169 м² | 1125 мм | 1120 мм | 250 мм | 245 мм | саморезы |
| AL-STS-1-1125х300-АА | 0.203 м² | 1125 мм | 1120 мм | 300 мм | 295 мм | саморезы |
| AL-STS-1-1125х325-АА | 0.220 м² | 1125 мм | 1120 мм | 325 мм | 320 мм | саморезы |
| AL-STS-1-1125х350-АА | 0.237 м² | 1125 мм | 1120 мм | 350 мм | 345 мм | саморезы |
| AL-STS-1-1125х400-АА | 0.271 м² | 1125 мм | 1120 мм | 400 мм | 395 мм | саморезы |
| AL-STS-1-1125х425-АА | 0.288 м² | 1125 мм | 1120 мм | 425 мм | 420 мм | саморезы |
| AL-STS-1-1125х450-АА | 0.305 м² | 1125 мм | 1120 мм | 450 мм | 445 мм | саморезы |
| AL-STS-1-1125х500-АА | 0.338 м² | 1125 мм | 1120 мм | 500 мм | 495 мм | саморезы |
| AL-STS-1-1125х525-АА | 0.355 м² | 1125 мм | 1120 мм | 525 мм | 520 мм | саморезы |
| AL-STS-1-1125х550-АА | 0.372 м² | 1125 мм | 1120 мм | 550 мм | 545 мм | саморезы |
| AL-STS-1-1125х600-АА | 0.406 м² | 1125 мм | 1120 мм | 600 мм | 595 мм | саморезы |
| AL-STS-1-1125х625-АА | 0.423 м² | 1125 мм | 1120 мм | 625 мм | 620 мм | саморезы |
| AL-STS-1-1125х650-АА | 0.440 м² | 1125 мм | 1120 мм | 650 мм | 645 мм | саморезы |
| AL-STS-1-1150х100-АА | 0.069 м² | 1150 мм | 1145 мм | 100 мм | 95 мм | саморезы |
| AL-STS-1-1150х125-АА | 0.086 м² | 1150 мм | 1145 мм | 125 мм | 120 мм | саморезы |
| AL-STS-1-1150х150-АА | 0.104 м² | 1150 мм | 1145 мм | 150 мм | 145 мм | саморезы |
| AL-STS-1-1150х200-АА | 0.138 м² | 1150 мм | 1145 мм | 200 мм | 195 мм | саморезы |
| AL-STS-1-1150х225-АА | 0.156 м² | 1150 мм | 1145 мм | 225 мм | 220 мм | саморезы |
| AL-STS-1-1150х250-АА | 0.173 м² | 1150 мм | 1145 мм | 250 мм | 245 мм | саморезы |
| AL-STS-1-1150х300-АА | 0.208 м² | 1150 мм | 1145 мм | 300 мм | 295 мм | саморезы |
| AL-STS-1-1150х325-АА | 0.225 м² | 1150 мм | 1145 мм | 325 мм | 320 мм | саморезы |
| AL-STS-1-1150х350-АА | 0.242 м² | 1150 мм | 1145 мм | 350 мм | 345 мм | саморезы |
| AL-STS-1-1150х400-АА | 0.277 м² | 1150 мм | 1145 мм | 400 мм | 395 мм | саморезы |
| AL-STS-1-1150х425-АА | 0.294 м² | 1150 мм | 1145 мм | 425 мм | 420 мм | саморезы |
| AL-STS-1-1150х450-АА | 0.311 м² | 1150 мм | 1145 мм | 450 мм | 445 мм | саморезы |
| AL-STS-1-1150х500-АА | 0.346 м² | 1150 мм | 1145 мм | 500 мм | 495 мм | саморезы |
| AL-STS-1-1150х525-АА | 0.363 м² | 1150 мм | 1145 мм | 525 мм | 520 мм | саморезы |
| AL-STS-1-1150х550-АА | 0.381 м² | 1150 мм | 1145 мм | 550 мм | 545 мм | саморезы |
| AL-STS-1-1150х600-АА | 0.415 м² | 1150 мм | 1145 мм | 600 мм | 595 мм | саморезы |
| AL-STS-1-1150х625-АА | 0.432 м² | 1150 мм | 1145 мм | 625 мм | 620 мм | саморезы |
| AL-STS-1-1150х650-АА | 0.450 м² | 1150 мм | 1145 мм | 650 мм | 645 мм | саморезы |
| AL-STS-1-1200х100-АА | 0.072 м² | 1200 мм | 1195 мм | 100 мм | 95 мм | саморезы |
| AL-STS-1-1200х125-АА | 0.090 м² | 1200 мм | 1195 мм | 125 мм | 120 мм | саморезы |
| AL-STS-1-1200х150-АА | 0.108 м² | 1200 мм | 1195 мм | 150 мм | 145 мм | саморезы |
| AL-STS-1-1200х200-АА | 0.144 м² | 1200 мм | 1195 мм | 200 мм | 195 мм | саморезы |
| AL-STS-1-1200х225-АА | 0.162 м² | 1200 мм | 1195 мм | 225 мм | 220 мм | саморезы |
| AL-STS-1-1200х250-АА | 0.180 м² | 1200 мм | 1195 мм | 250 мм | 245 мм | саморезы |
| AL-STS-1-1200х300-АА | 0.217 м² | 1200 мм | 1195 мм | 300 мм | 295 мм | саморезы |
| AL-STS-1-1200х325-АА | 0.235 м² | 1200 мм | 1195 мм | 325 мм | 320 мм | саморезы |
| AL-STS-1-1200х350-АА | 0.253 м² | 1200 мм | 1195 мм | 350 мм | 345 мм | саморезы |
| AL-STS-1-1200х400-АА | 0.289 м² | 1200 мм | 1195 мм | 400 мм | 395 мм | саморезы |
| AL-STS-1-1200х425-АА | 0.307 м² | 1200 мм | 1195 мм | 425 мм | 420 мм | саморезы |
| AL-STS-1-1200х450-АА | 0.325 м² | 1200 мм | 1195 мм | 450 мм | 445 мм | саморезы |
| AL-STS-1-1200х500-АА | 0.361 м² | 1200 мм | 1195 мм | 500 мм | 495 мм | саморезы |
| AL-STS-1-1200х525-АА | 0.379 м² | 1200 мм | 1195 мм | 525 мм | 520 мм | саморезы |
| AL-STS-1-1200х550-АА | 0.397 м² | 1200 мм | 1195 мм | 550 мм | 545 мм | саморезы |
| AL-STS-1-1200х600-АА | 0.433 м² | 1200 мм | 1195 мм | 600 мм | 595 мм | саморезы |
| AL-STS-1-1200х625-АА | 0.451 м² | 1200 мм | 1195 мм | 625 мм | 620 мм | саморезы |
| AL-STS-1-1200х650-АА | 0.469 м² | 1200 мм | 1195 мм | 650 мм | 645 мм | саморезы |
| AL-STS-1-1225х100-АА | 0.074 м² | 1225 мм | 1220 мм | 100 мм | 95 мм | саморезы |
| AL-STS-1-1225х125-АА | 0.092 м² | 1225 мм | 1220 мм | 125 мм | 120 мм | саморезы |
| AL-STS-1-1225х150-АА | 0.111 м² | 1225 мм | 1220 мм | 150 мм | 145 мм | саморезы |
| AL-STS-1-1225х200-АА | 0.147 м² | 1225 мм | 1220 мм | 200 мм | 195 мм | саморезы |
| AL-STS-1-1225х225-АА | 0.166 м² | 1225 мм | 1220 мм | 225 мм | 220 мм | саморезы |
| AL-STS-1-1225х250-АА | 0.184 м² | 1225 мм | 1220 мм | 250 мм | 245 мм | саморезы |
| AL-STS-1-1225х300-АА | 0.221 м² | 1225 мм | 1220 мм | 300 мм | 295 мм | саморезы |
| AL-STS-1-1225х325-АА | 0.240 м² | 1225 мм | 1220 мм | 325 мм | 320 мм | саморезы |
| AL-STS-1-1225х350-АА | 0.258 м² | 1225 мм | 1220 мм | 350 мм | 345 мм | саморезы |
| AL-STS-1-1225х400-АА | 0.295 м² | 1225 мм | 1220 мм | 400 мм | 395 мм | саморезы |
| AL-STS-1-1225х425-АА | 0.313 м² | 1225 мм | 1220 мм | 425 мм | 420 мм | саморезы |
| AL-STS-1-1225х450-АА | 0.332 м² | 1225 мм | 1220 мм | 450 мм | 445 мм | саморезы |
| AL-STS-1-1225х500-АА | 0.368 м² | 1225 мм | 1220 мм | 500 мм | 495 мм | саморезы |
| AL-STS-1-1225х525-АА | 0.387 м² | 1225 мм | 1220 мм | 525 мм | 520 мм | саморезы |
| AL-STS-1-1225х550-АА | 0.405 м² | 1225 мм | 1220 мм | 550 мм | 545 мм | саморезы |
| AL-STS-1-1225х600-АА | 0.442 м² | 1225 мм | 1220 мм | 600 мм | 595 мм | саморезы |
| AL-STS-1-1225х625-АА | 0.461 м² | 1225 мм | 1220 мм | 625 мм | 620 мм | саморезы |
| AL-STS-1-1225х650-АА | 0.479 м² | 1225 мм | 1220 мм | 650 мм | 645 мм | саморезы |
| AL-STS-1-1250х100-АА | 0.075 м² | 1250 мм | 1245 мм | 100 мм | 95 мм | саморезы |
| AL-STS-1-1250х125-АА | 0.094 м² | 1250 мм | 1245 мм | 125 мм | 120 мм | саморезы |
| AL-STS-1-1250х150-АА | 0.113 м² | 1250 мм | 1245 мм | 150 мм | 145 мм | саморезы |
| AL-STS-1-1250х200-АА | 0.150 м² | 1250 мм | 1245 мм | 200 мм | 195 мм | саморезы |
| AL-STS-1-1250х225-АА | 0.169 м² | 1250 мм | 1245 мм | 225 мм | 220 мм | саморезы |
| AL-STS-1-1250х250-АА | 0.188 м² | 1250 мм | 1245 мм | 250 мм | 245 мм | саморезы |
| AL-STS-1-1250х300-АА | 0.226 м² | 1250 мм | 1245 мм | 300 мм | 295 мм | саморезы |
| AL-STS-1-1250х325-АА | 0.244 м² | 1250 мм | 1245 мм | 325 мм | 320 мм | саморезы |
| AL-STS-1-1250х350-АА | 0.263 м² | 1250 мм | 1245 мм | 350 мм | 345 мм | саморезы |
| AL-STS-1-1250х400-АА | 0.301 м² | 1250 мм | 1245 мм | 400 мм | 395 мм | саморезы |
| AL-STS-1-1250х425-АА | 0.320 м² | 1250 мм | 1245 мм | 425 мм | 420 мм | саморезы |
| AL-STS-1-1250х450-АА | 0.338 м² | 1250 мм | 1245 мм | 450 мм | 445 мм | саморезы |
| AL-STS-1-1250х500-АА | 0.376 м² | 1250 мм | 1245 мм | 500 мм | 495 мм | саморезы |
| AL-STS-1-1250х525-АА | 0.395 м² | 1250 мм | 1245 мм | 525 мм | 520 мм | саморезы |
| AL-STS-1-1250х550-АА | 0.414 м² | 1250 мм | 1245 мм | 550 мм | 545 мм | саморезы |
| AL-STS-1-1250х600-АА | 0.451 м² | 1250 мм | 1245 мм | 600 мм | 595 мм | саморезы |
| AL-STS-1-1250х625-АА | 0.470 м² | 1250 мм | 1245 мм | 625 мм | 620 мм | саморезы |
| AL-STS-1-1250х650-АА | 0.489 м² | 1250 мм | 1245 мм | 650 мм | 645 мм | саморезы |
| AL-STS-1-1300х100-АА | 0.078 м² | 1300 мм | 1295 мм | 100 мм | 95 мм | саморезы |
| AL-STS-1-1300х125-АА | 0.098 м² | 1300 мм | 1295 мм | 125 мм | 120 мм | саморезы |
| AL-STS-1-1300х150-АА | 0.117 м² | 1300 мм | 1295 мм | 150 мм | 145 мм | саморезы |
| AL-STS-1-1300х200-АА | 0.156 м² | 1300 мм | 1295 мм | 200 мм | 195 мм | саморезы |
| AL-STS-1-1300х225-АА | 0.176 м² | 1300 мм | 1295 мм | 225 мм | 220 мм | саморезы |
| AL-STS-1-1300х250-АА | 0.196 м² | 1300 мм | 1295 мм | 250 мм | 245 мм | саморезы |
| AL-STS-1-1300х300-АА | 0.235 м² | 1300 мм | 1295 мм | 300 мм | 295 мм | саморезы |
| AL-STS-1-1300х325-АА | 0.254 м² | 1300 мм | 1295 мм | 325 мм | 320 мм | саморезы |
| AL-STS-1-1300х350-АА | 0.274 м² | 1300 мм | 1295 мм | 350 мм | 345 мм | саморезы |
| AL-STS-1-1300х400-АА | 0.313 м² | 1300 мм | 1295 мм | 400 мм | 395 мм | саморезы |
| AL-STS-1-1300х425-АА | 0.332 м² | 1300 мм | 1295 мм | 425 мм | 420 мм | саморезы |
| AL-STS-1-1300х450-АА | 0.352 м² | 1300 мм | 1295 мм | 450 мм | 445 мм | саморезы |
| AL-STS-1-1300х500-АА | 0.391 м² | 1300 мм | 1295 мм | 500 мм | 495 мм | саморезы |
| AL-STS-1-1300х525-АА | 0.411 м² | 1300 мм | 1295 мм | 525 мм | 520 мм | саморезы |
| AL-STS-1-1300х550-АА | 0.430 м² | 1300 мм | 1295 мм | 550 мм | 545 мм | саморезы |
| AL-STS-1-1300х600-АА | 0.469 м² | 1300 мм | 1295 мм | 600 мм | 595 мм | саморезы |
| AL-STS-1-1300х625-АА | 0.489 м² | 1300 мм | 1295 мм | 625 мм | 620 мм | саморезы |
| AL-STS-1-1300х650-АА | 0.508 м² | 1300 мм | 1295 мм | 650 мм | 645 мм | саморезы |
| AL-STS-1-1325х100-АА | 0.080 м² | 1325 мм | 1320 мм | 100 мм | 95 мм | саморезы |
| AL-STS-1-1325х125-АА | 0.100 м² | 1325 мм | 1320 мм | 125 мм | 120 мм | саморезы |
| AL-STS-1-1325х150-АА | 0.120 м² | 1325 мм | 1320 мм | 150 мм | 145 мм | саморезы |
| AL-STS-1-1325х200-АА | 0.159 м² | 1325 мм | 1320 мм | 200 мм | 195 мм | саморезы |
| AL-STS-1-1325х225-АА | 0.179 м² | 1325 мм | 1320 мм | 225 мм | 220 мм | саморезы |
| AL-STS-1-1325х250-АА | 0.199 м² | 1325 мм | 1320 мм | 250 мм | 245 мм | саморезы |
| AL-STS-1-1325х300-АА | 0.239 м² | 1325 мм | 1320 мм | 300 мм | 295 мм | саморезы |
| AL-STS-1-1325х325-АА | 0.259 м² | 1325 мм | 1320 мм | 325 мм | 320 мм | саморезы |
| AL-STS-1-1325х350-АА | 0.279 м² | 1325 мм | 1320 мм | 350 мм | 345 мм | саморезы |
| AL-STS-1-1325х400-АА | 0.319 м² | 1325 мм | 1320 мм | 400 мм | 395 мм | саморезы |
| AL-STS-1-1325х425-АА | 0.339 м² | 1325 мм | 1320 мм | 425 мм | 420 мм | саморезы |
| AL-STS-1-1325х450-АА | 0.359 м² | 1325 мм | 1320 мм | 450 мм | 445 мм | саморезы |
| AL-STS-1-1325х500-АА | 0.399 м² | 1325 мм | 1320 мм | 500 мм | 495 мм | саморезы |
| AL-STS-1-1325х525-АА | 0.418 м² | 1325 мм | 1320 мм | 525 мм | 520 мм | саморезы |
| AL-STS-1-1325х550-АА | 0.438 м² | 1325 мм | 1320 мм | 550 мм | 545 мм | саморезы |
| AL-STS-1-1325х600-АА | 0.478 м² | 1325 мм | 1320 мм | 600 мм | 595 мм | саморезы |
| AL-STS-1-1325х625-АА | 0.498 м² | 1325 мм | 1320 мм | 625 мм | 620 мм | саморезы |
| AL-STS-1-1325х650-АА | 0.518 м² | 1325 мм | 1320 мм | 650 мм | 645 мм | саморезы |
| AL-STS-1-1350х100-АА | 0.081 м² | 1350 мм | 1345 мм | 100 мм | 95 мм | саморезы |
| AL-STS-1-1350х125-АА | 0.102 м² | 1350 мм | 1345 мм | 125 мм | 120 мм | саморезы |
| AL-STS-1-1350х150-АА | 0.122 м² | 1350 мм | 1345 мм | 150 мм | 145 мм | саморезы |
| AL-STS-1-1350х200-АА | 0.162 м² | 1350 мм | 1345 мм | 200 мм | 195 мм | саморезы |
| AL-STS-1-1350х225-АА | 0.183 м² | 1350 мм | 1345 мм | 225 мм | 220 мм | саморезы |
| AL-STS-1-1350х250-АА | 0.203 м² | 1350 мм | 1345 мм | 250 мм | 245 мм | саморезы |
| AL-STS-1-1350х300-АА | 0.244 м² | 1350 мм | 1345 мм | 300 мм | 295 мм | саморезы |
| AL-STS-1-1350х325-АА | 0.264 м² | 1350 мм | 1345 мм | 325 мм | 320 мм | саморезы |
| AL-STS-1-1350х350-АА | 0.284 м² | 1350 мм | 1345 мм | 350 мм | 345 мм | саморезы |
| AL-STS-1-1350х400-АА | 0.325 м² | 1350 мм | 1345 мм | 400 мм | 395 мм | саморезы |
| AL-STS-1-1350х425-АА | 0.345 м² | 1350 мм | 1345 мм | 425 мм | 420 мм | саморезы |
| AL-STS-1-1350х450-АА | 0.365 м² | 1350 мм | 1345 мм | 450 мм | 445 мм | саморезы |
| AL-STS-1-1350х500-АА | 0.406 м² | 1350 мм | 1345 мм | 500 мм | 495 мм | саморезы |
| AL-STS-1-1350х525-АА | 0.426 м² | 1350 мм | 1345 мм | 525 мм | 520 мм | саморезы |
| AL-STS-1-1350х550-АА | 0.447 м² | 1350 мм | 1345 мм | 550 мм | 545 мм | саморезы |
| AL-STS-1-1350х600-АА | 0.487 м² | 1350 мм | 1345 мм | 600 мм | 595 мм | саморезы |
| AL-STS-1-1350х625-АА | 0.508 м² | 1350 мм | 1345 мм | 625 мм | 620 мм | саморезы |
| AL-STS-1-1350х650-АА | 0.528 м² | 1350 мм | 1345 мм | 650 мм | 645 мм | саморезы |
| AL-STS-1-1400х100-АА | 0.084 м² | 1400 мм | 1395 мм | 100 мм | 95 мм | саморезы |
| AL-STS-1-1400х125-АА | 0.105 м² | 1400 мм | 1395 мм | 125 мм | 120 мм | саморезы |
| AL-STS-1-1400х150-АА | 0.126 м² | 1400 мм | 1395 мм | 150 мм | 145 мм | саморезы |
| AL-STS-1-1400х200-АА | 0.168 м² | 1400 мм | 1395 мм | 200 мм | 195 мм | саморезы |
| AL-STS-1-1400х225-АА | 0.190 м² | 1400 мм | 1395 мм | 225 мм | 220 мм | саморезы |
| AL-STS-1-1400х250-АА | 0.211 м² | 1400 мм | 1395 мм | 250 мм | 245 мм | саморезы |
| AL-STS-1-1400х300-АА | 0.253 м² | 1400 мм | 1395 мм | 300 мм | 295 мм | саморезы |
| AL-STS-1-1400х325-АА | 0.274 м² | 1400 мм | 1395 мм | 325 мм | 320 мм | саморезы |
| AL-STS-1-1400х350-АА | 0.295 м² | 1400 мм | 1395 мм | 350 мм | 345 мм | саморезы |
| AL-STS-1-1400х400-АА | 0.337 м² | 1400 мм | 1395 мм | 400 мм | 395 мм | саморезы |
| AL-STS-1-1400х425-АА | 0.358 м² | 1400 мм | 1395 мм | 425 мм | 420 мм | саморезы |
| AL-STS-1-1400х450-АА | 0.379 м² | 1400 мм | 1395 мм | 450 мм | 445 мм | саморезы |
| AL-STS-1-1400х500-АА | 0.421 м² | 1400 мм | 1395 мм | 500 мм | 495 мм | саморезы |
| AL-STS-1-1400х525-АА | 0.442 м² | 1400 мм | 1395 мм | 525 мм | 520 мм | саморезы |
| AL-STS-1-1400х550-АА | 0.463 м² | 1400 мм | 1395 мм | 550 мм | 545 мм | саморезы |
| AL-STS-1-1400х600-АА | 0.505 м² | 1400 мм | 1395 мм | 600 мм | 595 мм | саморезы |
| AL-STS-1-1400х625-АА | 0.526 м² | 1400 мм | 1395 мм | 625 мм | 620 мм | саморезы |
| AL-STS-1-1400х650-АА | 0.547 м² | 1400 мм | 1395 мм | 650 мм | 645 мм | саморезы |
| AL-STS-1-1425х100-АА | 0.086 м² | 1425 мм | 1420 мм | 100 мм | 95 мм | саморезы |
| AL-STS-1-1425х125-АА | 0.107 м² | 1425 мм | 1420 мм | 125 мм | 120 мм | саморезы |
| AL-STS-1-1425х150-АА | 0.129 м² | 1425 мм | 1420 мм | 150 мм | 145 мм | саморезы |
| AL-STS-1-1425х200-АА | 0.171 м² | 1425 мм | 1420 мм | 200 мм | 195 мм | саморезы |
| AL-STS-1-1425х225-АА | 0.193 м² | 1425 мм | 1420 мм | 225 мм | 220 мм | саморезы |
| AL-STS-1-1425х250-АА | 0.214 м² | 1425 мм | 1420 мм | 250 мм | 245 мм | саморезы |
| AL-STS-1-1425х300-АА | 0.257 м² | 1425 мм | 1420 мм | 300 мм | 295 мм | саморезы |
| AL-STS-1-1425х325-АА | 0.279 м² | 1425 мм | 1420 мм | 325 мм | 320 мм | саморезы |
| AL-STS-1-1425х350-АА | 0.300 м² | 1425 мм | 1420 мм | 350 мм | 345 мм | саморезы |
| AL-STS-1-1425х400-АА | 0.343 м² | 1425 мм | 1420 мм | 400 мм | 395 мм | саморезы |
| AL-STS-1-1425х425-АА | 0.364 м² | 1425 мм | 1420 мм | 425 мм | 420 мм | саморезы |
| AL-STS-1-1425х450-АА | 0.386 м² | 1425 мм | 1420 мм | 450 мм | 445 мм | саморезы |
| AL-STS-1-1425х500-АА | 0.429 м² | 1425 мм | 1420 мм | 500 мм | 495 мм | саморезы |
| AL-STS-1-1425х525-АА | 0.450 м² | 1425 мм | 1420 мм | 525 мм | 520 мм | саморезы |
| AL-STS-1-1425х550-АА | 0.472 м² | 1425 мм | 1420 мм | 550 мм | 545 мм | саморезы |
| AL-STS-1-1425х600-АА | 0.514 м² | 1425 мм | 1420 мм | 600 мм | 595 мм | саморезы |
| AL-STS-1-1425х625-АА | 0.536 м² | 1425 мм | 1420 мм | 625 мм | 620 мм | саморезы |
| AL-STS-1-1425х650-АА | 0.557 м² | 1425 мм | 1420 мм | 650 мм | 645 мм | саморезы |
| AL-STS-1-1450х100-АА | 0.087 м² | 1450 мм | 1445 мм | 100 мм | 95 мм | саморезы |
| AL-STS-1-1450х125-АА | 0.109 м² | 1450 мм | 1445 мм | 125 мм | 120 мм | саморезы |
| AL-STS-1-1450х150-АА | 0.131 м² | 1450 мм | 1445 мм | 150 мм | 145 мм | саморезы |
| AL-STS-1-1450х200-АА | 0.174 м² | 1450 мм | 1445 мм | 200 мм | 195 мм | саморезы |
| AL-STS-1-1450х225-АА | 0.196 м² | 1450 мм | 1445 мм | 225 мм | 220 мм | саморезы |
| AL-STS-1-1450х250-АА | 0.218 м² | 1450 мм | 1445 мм | 250 мм | 245 мм | саморезы |
| AL-STS-1-1450х300-АА | 0.262 м² | 1450 мм | 1445 мм | 300 мм | 295 мм | саморезы |
| AL-STS-1-1450х325-АА | 0.284 м² | 1450 мм | 1445 мм | 325 мм | 320 мм | саморезы |
| AL-STS-1-1450х350-АА | 0.305 м² | 1450 мм | 1445 мм | 350 мм | 345 мм | саморезы |
| AL-STS-1-1450х400-АА | 0.349 м² | 1450 мм | 1445 мм | 400 мм | 395 мм | саморезы |
| AL-STS-1-1450х425-АА | 0.371 м² | 1450 мм | 1445 мм | 425 мм | 420 мм | саморезы |
| AL-STS-1-1450х450-АА | 0.393 м² | 1450 мм | 1445 мм | 450 мм | 445 мм | саморезы |
| AL-STS-1-1450х500-АА | 0.436 м² | 1450 мм | 1445 мм | 500 мм | 495 мм | саморезы |
| AL-STS-1-1450х525-АА | 0.458 м² | 1450 мм | 1445 мм | 525 мм | 520 мм | саморезы |
| AL-STS-1-1450х550-АА | 0.480 м² | 1450 мм | 1445 мм | 550 мм | 545 мм | саморезы |
| AL-STS-1-1450х600-АА | 0.523 м² | 1450 мм | 1445 мм | 600 мм | 595 мм | саморезы |
| AL-STS-1-1450х625-АА | 0.545 м² | 1450 мм | 1445 мм | 625 мм | 620 мм | саморезы |
| AL-STS-1-1450х650-АА | 0.567 м² | 1450 мм | 1445 мм | 650 мм | 645 мм | саморезы |
| AL-STS-1-1500х100-АА | 0.090 м² | 1500 мм | 1495 мм | 100 мм | 95 мм | саморезы |
| AL-STS-1-1500х125-АА | 0.113 м² | 1500 мм | 1495 мм | 125 мм | 120 мм | саморезы |
| AL-STS-1-1500х150-АА | 0.135 м² | 1500 мм | 1495 мм | 150 мм | 145 мм | саморезы |
| AL-STS-1-1500х200-АА | 0.180 м² | 1500 мм | 1495 мм | 200 мм | 195 мм | саморезы |
| AL-STS-1-1500х225-АА | 0.203 м² | 1500 мм | 1495 мм | 225 мм | 220 мм | саморезы |
| AL-STS-1-1500х250-АА | 0.226 м² | 1500 мм | 1495 мм | 250 мм | 245 мм | саморезы |
| AL-STS-1-1500х300-АА | 0.271 м² | 1500 мм | 1495 мм | 300 мм | 295 мм | саморезы |
| AL-STS-1-1500х325-АА | 0.293 м² | 1500 мм | 1495 мм | 325 мм | 320 мм | саморезы |
| AL-STS-1-1500х350-АА | 0.316 м² | 1500 мм | 1495 мм | 350 мм | 345 мм | саморезы |
| AL-STS-1-1500х400-АА | 0.361 м² | 1500 мм | 1495 мм | 400 мм | 395 мм | саморезы |
| AL-STS-1-1500х425-АА | 0.384 м² | 1500 мм | 1495 мм | 425 мм | 420 мм | саморезы |
| AL-STS-1-1500х450-АА | 0.406 м² | 1500 мм | 1495 мм | 450 мм | 445 мм | саморезы |
| AL-STS-1-1500х500-АА | 0.451 м² | 1500 мм | 1495 мм | 500 мм | 495 мм | саморезы |
| AL-STS-1-1500х525-АА | 0.474 м² | 1500 мм | 1495 мм | 525 мм | 520 мм | саморезы |
| AL-STS-1-1500х550-АА | 0.496 м² | 1500 мм | 1495 мм | 550 мм | 545 мм | саморезы |
| AL-STS-1-1500х600-АА | 0.541 м² | 1500 мм | 1495 мм | 600 мм | 595 мм | саморезы |
| AL-STS-1-1500х625-АА | 0.564 м² | 1500 мм | 1495 мм | 625 мм | 620 мм | саморезы |
| AL-STS-1-1500х650-АА | 0.587 м² | 1500 мм | 1495 мм | 650 мм | 645 мм | саморезы |
| AL-STS-1-100х100-Z-АА | 0.006 м² | 100 мм | 95 мм | 100 мм | 95 мм | скрытые защелки |
| AL-STS-1-125х100-Z-АА | 0.008 м² | 125 мм | 120 мм | 100 мм | 95 мм | скрытые защелки |
| AL-STS-1-125х125-Z-АА | 0.009 м² | 125 мм | 120 мм | 125 мм | 120 мм | скрытые защелки |
| AL-STS-1-150х100-Z-АА | 0.009 м² | 150 мм | 145 мм | 100 мм | 95 мм | скрытые защелки |
| AL-STS-1-150х125-Z-АА | 0.011 м² | 150 мм | 145 мм | 125 мм | 120 мм | скрытые защелки |
| AL-STS-1-150х150-Z-АА | 0.014 м² | 150 мм | 145 мм | 150 мм | 145 мм | скрытые защелки |
| AL-STS-1-200х100-Z-АА | 0.012 м² | 200 мм | 195 мм | 100 мм | 95 мм | скрытые защелки |
| AL-STS-1-200х125-Z-АА | 0.015 м² | 200 мм | 195 мм | 125 мм | 120 мм | скрытые защелки |
| AL-STS-1-200х150-Z-АА | 0.018 м² | 200 мм | 195 мм | 150 мм | 145 мм | скрытые защелки |
| AL-STS-1-200х200-Z-АА | 0.024 м² | 200 мм | 195 мм | 200 мм | 195 мм | скрытые защелки |
| AL-STS-1-225х100-Z-АА | 0.014 м² | 225 мм | 220 мм | 100 мм | 95 мм | скрытые защелки |
| AL-STS-1-225х125-Z-АА | 0.017 м² | 225 мм | 220 мм | 125 мм | 120 мм | скрытые защелки |
| AL-STS-1-225х150-Z-АА | 0.020 м² | 225 мм | 220 мм | 150 мм | 145 мм | скрытые защелки |
| AL-STS-1-225х200-Z-АА | 0.027 м² | 225 мм | 220 мм | 200 мм | 195 мм | скрытые защелки |
| AL-STS-1-225х225-Z-АА | 0.030 м² | 225 мм | 220 мм | 225 мм | 220 мм | скрытые защелки |
| AL-STS-1-250х100-Z-АА | 0.015 м² | 250 мм | 245 мм | 100 мм | 95 мм | скрытые защелки |
| AL-STS-1-250х125-Z-АА | 0.019 м² | 250 мм | 245 мм | 125 мм | 120 мм | скрытые защелки |
| AL-STS-1-250х150-Z-АА | 0.023 м² | 250 мм | 245 мм | 150 мм | 145 мм | скрытые защелки |
| AL-STS-1-250х200-Z-АА | 0.030 м² | 250 мм | 245 мм | 200 мм | 195 мм | скрытые защелки |
| AL-STS-1-250х225-Z-АА | 0.034 м² | 250 мм | 245 мм | 225 мм | 220 мм | скрытые защелки |
| AL-STS-1-250х250-Z-АА | 0.038 м² | 250 мм | 245 мм | 250 мм | 245 мм | скрытые защелки |
| AL-STS-1-300х100-Z-АА | 0.018 м² | 300 мм | 295 мм | 100 мм | 95 мм | скрытые защелки |
| AL-STS-1-300х125-Z-АА | 0.023 м² | 300 мм | 295 мм | 125 мм | 120 мм | скрытые защелки |
| AL-STS-1-300х150-Z-АА | 0.027 м² | 300 мм | 295 мм | 150 мм | 145 мм | скрытые защелки |
| AL-STS-1-300х200-Z-АА | 0.036 м² | 300 мм | 295 мм | 200 мм | 195 мм | скрытые защелки |
| AL-STS-1-300х225-Z-АА | 0.041 м² | 300 мм | 295 мм | 225 мм | 220 мм | скрытые защелки |
| AL-STS-1-300х250-Z-АА | 0.045 м² | 300 мм | 295 мм | 250 мм | 245 мм | скрытые защелки |
| AL-STS-1-300х300-Z-АА | 0.054 м² | 300 мм | 295 мм | 300 мм | 295 мм | скрытые защелки |
| AL-STS-1-325х100-Z-АА | 0.020 м² | 325 мм | 320 мм | 100 мм | 95 мм | скрытые защелки |
| AL-STS-1-325х125-Z-АА | 0.024 м² | 325 мм | 320 мм | 125 мм | 120 мм | скрытые защелки |
| AL-STS-1-325х150-Z-АА | 0.029 м² | 325 мм | 320 мм | 150 мм | 145 мм | скрытые защелки |
| AL-STS-1-325х200-Z-АА | 0.039 м² | 325 мм | 320 мм | 200 мм | 195 мм | скрытые защелки |
| AL-STS-1-325х225-Z-АА | 0.044 м² | 325 мм | 320 мм | 225 мм | 220 мм | скрытые защелки |
| AL-STS-1-325х250-Z-АА | 0.049 м² | 325 мм | 320 мм | 250 мм | 245 мм | скрытые защелки |
| AL-STS-1-325х300-Z-АА | 0.059 м² | 325 мм | 320 мм | 300 мм | 295 мм | скрытые защелки |
| AL-STS-1-325х325-Z-АА | 0.064 м² | 325 мм | 320 мм | 325 мм | 320 мм | скрытые защелки |
| AL-STS-1-350х100-Z-АА | 0.021 м² | 350 мм | 345 мм | 100 мм | 95 мм | скрытые защелки |
| AL-STS-1-350х125-Z-АА | 0.026 м² | 350 мм | 345 мм | 125 мм | 120 мм | скрытые защелки |
| AL-STS-1-350х150-Z-АА | 0.032 м² | 350 мм | 345 мм | 150 мм | 145 мм | скрытые защелки |
| AL-STS-1-350х200-Z-АА | 0.042 м² | 350 мм | 345 мм | 200 мм | 195 мм | скрытые защелки |
| AL-STS-1-350х225-Z-АА | 0.047 м² | 350 мм | 345 мм | 225 мм | 220 мм | скрытые защелки |
| AL-STS-1-350х250-Z-АА | 0.053 м² | 350 мм | 345 мм | 250 мм | 245 мм | скрытые защелки |
| AL-STS-1-350х300-Z-АА | 0.063 м² | 350 мм | 345 мм | 300 мм | 295 мм | скрытые защелки |
| AL-STS-1-350х325-Z-АА | 0.068 м² | 350 мм | 345 мм | 325 мм | 320 мм | скрытые защелки |
| AL-STS-1-350х350-Z-АА | 0.074 м² | 350 мм | 345 мм | 350 мм | 345 мм | скрытые защелки |
| AL-STS-1-400х100-Z-АА | 0.024 м² | 400 мм | 395 мм | 100 мм | 95 мм | скрытые защелки |
| AL-STS-1-400х125-Z-АА | 0.030 м² | 400 мм | 395 мм | 125 мм | 120 мм | скрытые защелки |
| AL-STS-1-400х150-Z-АА | 0.036 м² | 400 мм | 395 мм | 150 мм | 145 мм | скрытые защелки |
| AL-STS-1-400х200-Z-АА | 0.048 м² | 400 мм | 395 мм | 200 мм | 195 мм | скрытые защелки |
| AL-STS-1-400х225-Z-АА | 0.054 м² | 400 мм | 395 мм | 225 мм | 220 мм | скрытые защелки |
| AL-STS-1-400х250-Z-АА | 0.060 м² | 400 мм | 395 мм | 250 мм | 245 мм | скрытые защелки |
| AL-STS-1-400х300-Z-АА | 0.072 м² | 400 мм | 395 мм | 300 мм | 295 мм | скрытые защелки |
| AL-STS-1-400х325-Z-АА | 0.078 м² | 400 мм | 395 мм | 325 мм | 320 мм | скрытые защелки |
| AL-STS-1-400х350-Z-АА | 0.084 м² | 400 мм | 395 мм | 350 мм | 345 мм | скрытые защелки |
| AL-STS-1-400х400-Z-АА | 0.096 м² | 400 мм | 395 мм | 400 мм | 395 мм | скрытые защелки |
| AL-STS-1-425х100-Z-АА | 0.026 м² | 425 мм | 420 мм | 100 мм | 95 мм | скрытые защелки |
| AL-STS-1-425х125-Z-АА | 0.032 м² | 425 мм | 420 мм | 125 мм | 120 мм | скрытые защелки |
| AL-STS-1-425х150-Z-АА | 0.038 м² | 425 мм | 420 мм | 150 мм | 145 мм | скрытые защелки |
| AL-STS-1-425х200-Z-АА | 0.051 м² | 425 мм | 420 мм | 200 мм | 195 мм | скрытые защелки |
| AL-STS-1-425х225-Z-АА | 0.058 м² | 425 мм | 420 мм | 225 мм | 220 мм | скрытые защелки |
| AL-STS-1-425х250-Z-АА | 0.064 м² | 425 мм | 420 мм | 250 мм | 245 мм | скрытые защелки |
| AL-STS-1-425х300-Z-АА | 0.077 м² | 425 мм | 420 мм | 300 мм | 295 мм | скрытые защелки |
| AL-STS-1-425х325-Z-АА | 0.083 м² | 425 мм | 420 мм | 325 мм | 320 мм | скрытые защелки |
| AL-STS-1-425х350-Z-АА | 0.089 м² | 425 мм | 420 мм | 350 мм | 345 мм | скрытые защелки |
| AL-STS-1-425х400-Z-АА | 0.102 м² | 425 мм | 420 мм | 400 мм | 395 мм | скрытые защелки |
| AL-STS-1-425х425-Z-АА | 0.109 м² | 425 мм | 420 мм | 425 мм | 420 мм | скрытые защелки |
| AL-STS-1-450х100-Z-АА | 0.027 м² | 450 мм | 445 мм | 100 мм | 95 мм | скрытые защелки |
| AL-STS-1-450х125-Z-АА | 0.034 м² | 450 мм | 445 мм | 125 мм | 120 мм | скрытые защелки |
| AL-STS-1-450х150-Z-АА | 0.041 м² | 450 мм | 445 мм | 150 мм | 145 мм | скрытые защелки |
| AL-STS-1-450х200-Z-АА | 0.054 м² | 450 мм | 445 мм | 200 мм | 195 мм | скрытые защелки |
| AL-STS-1-450х225-Z-АА | 0.061 м² | 450 мм | 445 мм | 225 мм | 220 мм | скрытые защелки |
| AL-STS-1-450х250-Z-АА | 0.068 м² | 450 мм | 445 мм | 250 мм | 245 мм | скрытые защелки |
| AL-STS-1-450х300-Z-АА | 0.081 м² | 450 мм | 445 мм | 300 мм | 295 мм | скрытые защелки |
| AL-STS-1-450х325-Z-АА | 0.088 м² | 450 мм | 445 мм | 325 мм | 320 мм | скрытые защелки |
| AL-STS-1-450х350-Z-АА | 0.095 м² | 450 мм | 445 мм | 350 мм | 345 мм | скрытые защелки |
| AL-STS-1-450х400-Z-АА | 0.108 м² | 450 мм | 445 мм | 400 мм | 395 мм | скрытые защелки |
| AL-STS-1-450х425-Z-АА | 0.115 м² | 450 мм | 445 мм | 425 мм | 420 мм | скрытые защелки |
| AL-STS-1-450х450-Z-АА | 0.122 м² | 450 мм | 445 мм | 450 мм | 445 мм | скрытые защелки |
| AL-STS-1-500х100-Z-АА | 0.030 м² | 500 мм | 495 мм | 100 мм | 95 мм | скрытые защелки |
| AL-STS-1-500х125-Z-АА | 0.038 м² | 500 мм | 495 мм | 125 мм | 120 мм | скрытые защелки |
| AL-STS-1-500х150-Z-АА | 0.045 м² | 500 мм | 495 мм | 150 мм | 145 мм | скрытые защелки |
| AL-STS-1-500х200-Z-АА | 0.060 м² | 500 мм | 495 мм | 200 мм | 195 мм | скрытые защелки |
| AL-STS-1-500х225-Z-АА | 0.068 м² | 500 мм | 495 мм | 225 мм | 220 мм | скрытые защелки |
| AL-STS-1-500х250-Z-АА | 0.075 м² | 500 мм | 495 мм | 250 мм | 245 мм | скрытые защелки |
| AL-STS-1-500х300-Z-АА | 0.090 м² | 500 мм | 495 мм | 300 мм | 295 мм | скрытые защелки |
| AL-STS-1-500х325-Z-АА | 0.098 м² | 500 мм | 495 мм | 325 мм | 320 мм | скрытые защелки |
| AL-STS-1-500х350-Z-АА | 0.105 м² | 500 мм | 495 мм | 350 мм | 345 мм | скрытые защелки |
| AL-STS-1-500х400-Z-АА | 0.120 м² | 500 мм | 495 мм | 400 мм | 395 мм | скрытые защелки |
| AL-STS-1-500х425-Z-АА | 0.128 м² | 500 мм | 495 мм | 425 мм | 420 мм | скрытые защелки |
| AL-STS-1-500х450-Z-АА | 0.135 м² | 500 мм | 495 мм | 450 мм | 445 мм | скрытые защелки |
| AL-STS-1-500х500-Z-АА | 0.150 м² | 500 мм | 495 мм | 500 мм | 495 мм | скрытые защелки |
| AL-STS-1-525х100-Z-АА | 0.032 м² | 525 мм | 520 мм | 100 мм | 95 мм | скрытые защелки |
| AL-STS-1-525х125-Z-АА | 0.039 м² | 525 мм | 520 мм | 125 мм | 120 мм | скрытые защелки |
| AL-STS-1-525х150-Z-АА | 0.047 м² | 525 мм | 520 мм | 150 мм | 145 мм | скрытые защелки |
| AL-STS-1-525х200-Z-АА | 0.063 м² | 525 мм | 520 мм | 200 мм | 195 мм | скрытые защелки |
| AL-STS-1-525х225-Z-АА | 0.071 м² | 525 мм | 520 мм | 225 мм | 220 мм | скрытые защелки |
| AL-STS-1-525х250-Z-АА | 0.079 м² | 525 мм | 520 мм | 250 мм | 245 мм | скрытые защелки |
| AL-STS-1-525х300-Z-АА | 0.095 м² | 525 мм | 520 мм | 300 мм | 295 мм | скрытые защелки |
| AL-STS-1-525х325-Z-АА | 0.103 м² | 525 мм | 520 мм | 325 мм | 320 мм | скрытые защелки |
| AL-STS-1-525х350-Z-АА | 0.111 м² | 525 мм | 520 мм | 350 мм | 345 мм | скрытые защелки |
| AL-STS-1-525х400-Z-АА | 0.126 м² | 525 мм | 520 мм | 400 мм | 395 мм | скрытые защелки |
| AL-STS-1-525х425-Z-АА | 0.134 м² | 525 мм | 520 мм | 425 мм | 420 мм | скрытые защелки |
| AL-STS-1-525х450-Z-АА | 0.142 м² | 525 мм | 520 мм | 450 мм | 445 мм | скрытые защелки |
| AL-STS-1-525х500-Z-АА | 0.158 м² | 525 мм | 520 мм | 500 мм | 495 мм | скрытые защелки |
| AL-STS-1-525х525-Z-АА | 0.166 м² | 525 мм | 520 мм | 525 мм | 520 мм | скрытые защелки |
| AL-STS-1-550х100-Z-АА | 0.033 м² | 550 мм | 545 мм | 100 мм | 95 мм | скрытые защелки |
| AL-STS-1-550х125-Z-АА | 0.041 м² | 550 мм | 545 мм | 125 мм | 120 мм | скрытые защелки |
| AL-STS-1-550х150-Z-АА | 0.050 м² | 550 мм | 545 мм | 150 мм | 145 мм | скрытые защелки |
| AL-STS-1-550х200-Z-АА | 0.066 м² | 550 мм | 545 мм | 200 мм | 195 мм | скрытые защелки |
| AL-STS-1-550х225-Z-АА | 0.074 м² | 550 мм | 545 мм | 225 мм | 220 мм | скрытые защелки |
| AL-STS-1-550х250-Z-АА | 0.083 м² | 550 мм | 545 мм | 250 мм | 245 мм | скрытые защелки |
| AL-STS-1-550х300-Z-АА | 0.099 м² | 550 мм | 545 мм | 300 мм | 295 мм | скрытые защелки |
| AL-STS-1-550х325-Z-АА | 0.108 м² | 550 мм | 545 мм | 325 мм | 320 мм | скрытые защелки |
| AL-STS-1-550х350-Z-АА | 0.116 м² | 550 мм | 545 мм | 350 мм | 345 мм | скрытые защелки |
| AL-STS-1-550х400-Z-АА | 0.132 м² | 550 мм | 545 мм | 400 мм | 395 мм | скрытые защелки |
| AL-STS-1-550х425-Z-АА | 0.141 м² | 550 мм | 545 мм | 425 мм | 420 мм | скрытые защелки |
| AL-STS-1-550х450-Z-АА | 0.149 м² | 550 мм | 545 мм | 450 мм | 445 мм | скрытые защелки |
| AL-STS-1-550х500-Z-АА | 0.165 м² | 550 мм | 545 мм | 500 мм | 495 мм | скрытые защелки |
| AL-STS-1-550х525-Z-АА | 0.174 м² | 550 мм | 545 мм | 525 мм | 520 мм | скрытые защелки |
| AL-STS-1-550х550-Z-АА | 0.182 м² | 550 мм | 545 мм | 550 мм | 545 мм | скрытые защелки |
| AL-STS-1-600х100-Z-АА | 0.036 м² | 600 мм | 595 мм | 100 мм | 95 мм | скрытые защелки |
| AL-STS-1-600х125-Z-АА | 0.045 м² | 600 мм | 595 мм | 125 мм | 120 мм | скрытые защелки |
| AL-STS-1-600х150-Z-АА | 0.054 м² | 600 мм | 595 мм | 150 мм | 145 мм | скрытые защелки |
| AL-STS-1-600х200-Z-АА | 0.072 м² | 600 мм | 595 мм | 200 мм | 195 мм | скрытые защелки |
| AL-STS-1-600х225-Z-АА | 0.081 м² | 600 мм | 595 мм | 225 мм | 220 мм | скрытые защелки |
| AL-STS-1-600х250-Z-АА | 0.090 м² | 600 мм | 595 мм | 250 мм | 245 мм | скрытые защелки |
| AL-STS-1-600х300-Z-АА | 0.108 м² | 600 мм | 595 мм | 300 мм | 295 мм | скрытые защелки |
| AL-STS-1-600х325-Z-АА | 0.117 м² | 600 мм | 595 мм | 325 мм | 320 мм | скрытые защелки |
| AL-STS-1-600х350-Z-АА | 0.126 м² | 600 мм | 595 мм | 350 мм | 345 мм | скрытые защелки |
| AL-STS-1-600х400-Z-АА | 0.144 м² | 600 мм | 595 мм | 400 мм | 395 мм | скрытые защелки |
| AL-STS-1-600х425-Z-АА | 0.153 м² | 600 мм | 595 мм | 425 мм | 420 мм | скрытые защелки |
| AL-STS-1-600х450-Z-АА | 0.162 м² | 600 мм | 595 мм | 450 мм | 445 мм | скрытые защелки |
| AL-STS-1-600х500-Z-АА | 0.180 м² | 600 мм | 595 мм | 500 мм | 495 мм | скрытые защелки |
| AL-STS-1-600х525-Z-АА | 0.190 м² | 600 мм | 595 мм | 525 мм | 520 мм | скрытые защелки |
| AL-STS-1-600х550-Z-АА | 0.199 м² | 600 мм | 595 мм | 550 мм | 545 мм | скрытые защелки |
| AL-STS-1-600х600-Z-АА | 0.217 м² | 600 мм | 595 мм | 600 мм | 595 мм | скрытые защелки |
| AL-STS-1-625х100-Z-АА | 0.038 м² | 625 мм | 620 мм | 100 мм | 95 мм | скрытые защелки |
| AL-STS-1-625х125-Z-АА | 0.047 м² | 625 мм | 620 мм | 125 мм | 120 мм | скрытые защелки |
| AL-STS-1-625х150-Z-АА | 0.056 м² | 625 мм | 620 мм | 150 мм | 145 мм | скрытые защелки |
| AL-STS-1-625х200-Z-АА | 0.075 м² | 625 мм | 620 мм | 200 мм | 195 мм | скрытые защелки |
| AL-STS-1-625х225-Z-АА | 0.085 м² | 625 мм | 620 мм | 225 мм | 220 мм | скрытые защелки |
| AL-STS-1-625х250-Z-АА | 0.094 м² | 625 мм | 620 мм | 250 мм | 245 мм | скрытые защелки |
| AL-STS-1-625х300-Z-АА | 0.113 м² | 625 мм | 620 мм | 300 мм | 295 мм | скрытые защелки |
| AL-STS-1-625х325-Z-АА | 0.122 м² | 625 мм | 620 мм | 325 мм | 320 мм | скрытые защелки |
| AL-STS-1-625х350-Z-АА | 0.132 м² | 625 мм | 620 мм | 350 мм | 345 мм | скрытые защелки |
| AL-STS-1-625х400-Z-АА | 0.150 м² | 625 мм | 620 мм | 400 мм | 395 мм | скрытые защелки |
| AL-STS-1-625х425-Z-АА | 0.160 м² | 625 мм | 620 мм | 425 мм | 420 мм | скрытые защелки |
| AL-STS-1-625х450-Z-АА | 0.169 м² | 625 мм | 620 мм | 450 мм | 445 мм | скрытые защелки |
| AL-STS-1-625х500-Z-АА | 0.188 м² | 625 мм | 620 мм | 500 мм | 495 мм | скрытые защелки |
| AL-STS-1-625х525-Z-АА | 0.197 м² | 625 мм | 620 мм | 525 мм | 520 мм | скрытые защелки |
| AL-STS-1-625х550-Z-АА | 0.207 м² | 625 мм | 620 мм | 550 мм | 545 мм | скрытые защелки |
| AL-STS-1-625х600-Z-АА | 0.226 м² | 625 мм | 620 мм | 600 мм | 595 мм | скрытые защелки |
| AL-STS-1-625х625-Z-АА | 0.235 м² | 625 мм | 620 мм | 625 мм | 620 мм | скрытые защелки |
| AL-STS-1-650х100-Z-АА | 0.039 м² | 650 мм | 645 мм | 100 мм | 95 мм | скрытые защелки |
| AL-STS-1-650х125-Z-АА | 0.049 м² | 650 мм | 645 мм | 125 мм | 120 мм | скрытые защелки |
| AL-STS-1-650х150-Z-АА | 0.059 м² | 650 мм | 645 мм | 150 мм | 145 мм | скрытые защелки |
| AL-STS-1-650х200-Z-АА | 0.078 м² | 650 мм | 645 мм | 200 мм | 195 мм | скрытые защелки |
| AL-STS-1-650х225-Z-АА | 0.088 м² | 650 мм | 645 мм | 225 мм | 220 мм | скрытые защелки |
| AL-STS-1-650х250-Z-АА | 0.098 м² | 650 мм | 645 мм | 250 мм | 245 мм | скрытые защелки |
| AL-STS-1-650х300-Z-АА | 0.117 м² | 650 мм | 645 мм | 300 мм | 295 мм | скрытые защелки |
| AL-STS-1-650х325-Z-АА | 0.127 м² | 650 мм | 645 мм | 325 мм | 320 мм | скрытые защелки |
| AL-STS-1-650х350-Z-АА | 0.137 м² | 650 мм | 645 мм | 350 мм | 345 мм | скрытые защелки |
| AL-STS-1-650х400-Z-АА | 0.156 м² | 650 мм | 645 мм | 400 мм | 395 мм | скрытые защелки |
| AL-STS-1-650х425-Z-АА | 0.166 м² | 650 мм | 645 мм | 425 мм | 420 мм | скрытые защелки |
| AL-STS-1-650х450-Z-АА | 0.176 м² | 650 мм | 645 мм | 450 мм | 445 мм | скрытые защелки |
| AL-STS-1-650х500-Z-АА | 0.196 м² | 650 мм | 645 мм | 500 мм | 495 мм | скрытые защелки |
| AL-STS-1-650х525-Z-АА | 0.205 м² | 650 мм | 645 мм | 525 мм | 520 мм | скрытые защелки |
| AL-STS-1-650х550-Z-АА | 0.215 м² | 650 мм | 645 мм | 550 мм | 545 мм | скрытые защелки |
| AL-STS-1-650х600-Z-АА | 0.235 м² | 650 мм | 645 мм | 600 мм | 595 мм | скрытые защелки |
| AL-STS-1-650х625-Z-АА | 0.244 м² | 650 мм | 645 мм | 625 мм | 620 мм | скрытые защелки |
| AL-STS-1-650х650-Z-АА | 0.254 м² | 650 мм | 645 мм | 650 мм | 645 мм | скрытые защелки |
| AL-STS-1-700х100-Z-АА | 0.042 м² | 700 мм | 695 мм | 100 мм | 95 мм | скрытые защелки |
| AL-STS-1-700х125-Z-АА | 0.053 м² | 700 мм | 695 мм | 125 мм | 120 мм | скрытые защелки |
| AL-STS-1-700х150-Z-АА | 0.063 м² | 700 мм | 695 мм | 150 мм | 145 мм | скрытые защелки |
| AL-STS-1-700х200-Z-АА | 0.084 м² | 700 мм | 695 мм | 200 мм | 195 мм | скрытые защелки |
| AL-STS-1-700х225-Z-АА | 0.095 м² | 700 мм | 695 мм | 225 мм | 220 мм | скрытые защелки |
| AL-STS-1-700х250-Z-АА | 0.105 м² | 700 мм | 695 мм | 250 мм | 245 мм | скрытые защелки |
| AL-STS-1-700х300-Z-АА | 0.126 м² | 700 мм | 695 мм | 300 мм | 295 мм | скрытые защелки |
| AL-STS-1-700х325-Z-АА | 0.137 м² | 700 мм | 695 мм | 325 мм | 320 мм | скрытые защелки |
| AL-STS-1-700х350-Z-АА | 0.147 м² | 700 мм | 695 мм | 350 мм | 345 мм | скрытые защелки |
| AL-STS-1-700х400-Z-АА | 0.168 м² | 700 мм | 695 мм | 400 мм | 395 мм | скрытые защелки |
| AL-STS-1-700х425-Z-АА | 0.179 м² | 700 мм | 695 мм | 425 мм | 420 мм | скрытые защелки |
| AL-STS-1-700х450-Z-АА | 0.190 м² | 700 мм | 695 мм | 450 мм | 445 мм | скрытые защелки |
| AL-STS-1-700х500-Z-АА | 0.211 м² | 700 мм | 695 мм | 500 мм | 495 мм | скрытые защелки |
| AL-STS-1-700х525-Z-АА | 0.221 м² | 700 мм | 695 мм | 525 мм | 520 мм | скрытые защелки |
| AL-STS-1-700х550-Z-АА | 0.232 м² | 700 мм | 695 мм | 550 мм | 545 мм | скрытые защелки |
| AL-STS-1-700х600-Z-АА | 0.253 м² | 700 мм | 695 мм | 600 мм | 595 мм | скрытые защелки |
| AL-STS-1-700х625-Z-АА | 0.263 м² | 700 мм | 695 мм | 625 мм | 620 мм | скрытые защелки |
| AL-STS-1-700х650-Z-АА | 0.274 м² | 700 мм | 695 мм | 650 мм | 645 мм | скрытые защелки |
| AL-STS-1-725х100-Z-АА | 0.044 м² | 725 мм | 720 мм | 100 мм | 95 мм | скрытые защелки |
| AL-STS-1-725х125-Z-АА | 0.055 м² | 725 мм | 720 мм | 125 мм | 120 мм | скрытые защелки |
| AL-STS-1-725х150-Z-АА | 0.065 м² | 725 мм | 720 мм | 150 мм | 145 мм | скрытые защелки |
| AL-STS-1-725х200-Z-АА | 0.087 м² | 725 мм | 720 мм | 200 мм | 195 мм | скрытые защелки |
| AL-STS-1-725х225-Z-АА | 0.098 м² | 725 мм | 720 мм | 225 мм | 220 мм | скрытые защелки |
| AL-STS-1-725х250-Z-АА | 0.109 м² | 725 мм | 720 мм | 250 мм | 245 мм | скрытые защелки |
| AL-STS-1-725х300-Z-АА | 0.131 м² | 725 мм | 720 мм | 300 мм | 295 мм | скрытые защелки |
| AL-STS-1-725х325-Z-АА | 0.142 м² | 725 мм | 720 мм | 325 мм | 320 мм | скрытые защелки |
| AL-STS-1-725х350-Z-АА | 0.153 м² | 725 мм | 720 мм | 350 мм | 345 мм | скрытые защелки |
| AL-STS-1-725х400-Z-АА | 0.174 м² | 725 мм | 720 мм | 400 мм | 395 мм | скрытые защелки |
| AL-STS-1-725х425-Z-АА | 0.185 м² | 725 мм | 720 мм | 425 мм | 420 мм | скрытые защелки |
| AL-STS-1-725х450-Z-АА | 0.196 м² | 725 мм | 720 мм | 450 мм | 445 мм | скрытые защелки |
| AL-STS-1-725х500-Z-АА | 0.218 м² | 725 мм | 720 мм | 500 мм | 495 мм | скрытые защелки |
| AL-STS-1-725х525-Z-АА | 0.229 м² | 725 мм | 720 мм | 525 мм | 520 мм | скрытые защелки |
| AL-STS-1-725х550-Z-АА | 0.240 м² | 725 мм | 720 мм | 550 мм | 545 мм | скрытые защелки |
| AL-STS-1-725х600-Z-АА | 0.262 м² | 725 мм | 720 мм | 600 мм | 595 мм | скрытые защелки |
| AL-STS-1-725х625-Z-АА | 0.273 м² | 725 мм | 720 мм | 625 мм | 620 мм | скрытые защелки |
| AL-STS-1-725х650-Z-АА | 0.284 м² | 725 мм | 720 мм | 650 мм | 645 мм | скрытые защелки |
| AL-STS-1-750х100-Z-АА | 0.045 м² | 750 мм | 745 мм | 100 мм | 95 мм | скрытые защелки |
| AL-STS-1-750х125-Z-АА | 0.056 м² | 750 мм | 745 мм | 125 мм | 120 мм | скрытые защелки |
| AL-STS-1-750х150-Z-АА | 0.068 м² | 750 мм | 745 мм | 150 мм | 145 мм | скрытые защелки |
| AL-STS-1-750х200-Z-АА | 0.090 м² | 750 мм | 745 мм | 200 мм | 195 мм | скрытые защелки |
| AL-STS-1-750х225-Z-АА | 0.102 м² | 750 мм | 745 мм | 225 мм | 220 мм | скрытые защелки |
| AL-STS-1-750х250-Z-АА | 0.113 м² | 750 мм | 745 мм | 250 мм | 245 мм | скрытые защелки |
| AL-STS-1-750х300-Z-АА | 0.135 м² | 750 мм | 745 мм | 300 мм | 295 мм | скрытые защелки |
| AL-STS-1-750х325-Z-АА | 0.147 м² | 750 мм | 745 мм | 325 мм | 320 мм | скрытые защелки |
| AL-STS-1-750х350-Z-АА | 0.158 м² | 750 мм | 745 мм | 350 мм | 345 мм | скрытые защелки |
| AL-STS-1-750х400-Z-АА | 0.180 м² | 750 мм | 745 мм | 400 мм | 395 мм | скрытые защелки |
| AL-STS-1-750х425-Z-АА | 0.192 м² | 750 мм | 745 мм | 425 мм | 420 мм | скрытые защелки |
| AL-STS-1-750х450-Z-АА | 0.203 м² | 750 мм | 745 мм | 450 мм | 445 мм | скрытые защелки |
| AL-STS-1-750х500-Z-АА | 0.226 м² | 750 мм | 745 мм | 500 мм | 495 мм | скрытые защелки |
| AL-STS-1-750х525-Z-АА | 0.237 м² | 750 мм | 745 мм | 525 мм | 520 мм | скрытые защелки |
| AL-STS-1-750х550-Z-АА | 0.248 м² | 750 мм | 745 мм | 550 мм | 545 мм | скрытые защелки |
| AL-STS-1-750х600-Z-АА | 0.271 м² | 750 мм | 745 мм | 600 мм | 595 мм | скрытые защелки |
| AL-STS-1-750х625-Z-АА | 0.282 м² | 750 мм | 745 мм | 625 мм | 620 мм | скрытые защелки |
| AL-STS-1-750х650-Z-АА | 0.293 м² | 750 мм | 745 мм | 650 мм | 645 мм | скрытые защелки |
| AL-STS-1-800х100-Z-АА | 0.048 м² | 800 мм | 795 мм | 100 мм | 95 мм | скрытые защелки |
| AL-STS-1-800х125-Z-АА | 0.060 м² | 800 мм | 795 мм | 125 мм | 120 мм | скрытые защелки |
| AL-STS-1-800х150-Z-АА | 0.072 м² | 800 мм | 795 мм | 150 мм | 145 мм | скрытые защелки |
| AL-STS-1-800х200-Z-АА | 0.096 м² | 800 мм | 795 мм | 200 мм | 195 мм | скрытые защелки |
| AL-STS-1-800х225-Z-АА | 0.108 м² | 800 мм | 795 мм | 225 мм | 220 мм | скрытые защелки |
| AL-STS-1-800х250-Z-АА | 0.120 м² | 800 мм | 795 мм | 250 мм | 245 мм | скрытые защелки |
| AL-STS-1-800х300-Z-АА | 0.144 м² | 800 мм | 795 мм | 300 мм | 295 мм | скрытые защелки |
| AL-STS-1-800х325-Z-АА | 0.156 м² | 800 мм | 795 мм | 325 мм | 320 мм | скрытые защелки |
| AL-STS-1-800х350-Z-АА | 0.168 м² | 800 мм | 795 мм | 350 мм | 345 мм | скрытые защелки |
| AL-STS-1-800х400-Z-АА | 0.193 м² | 800 мм | 795 мм | 400 мм | 395 мм | скрытые защелки |
| AL-STS-1-800х425-Z-АА | 0.205 м² | 800 мм | 795 мм | 425 мм | 420 мм | скрытые защелки |
| AL-STS-1-800х450-Z-АА | 0.217 м² | 800 мм | 795 мм | 450 мм | 445 мм | скрытые защелки |
| AL-STS-1-800х500-Z-АА | 0.241 м² | 800 мм | 795 мм | 500 мм | 495 мм | скрытые защелки |
| AL-STS-1-800х525-Z-АА | 0.253 м² | 800 мм | 795 мм | 525 мм | 520 мм | скрытые защелки |
| AL-STS-1-800х550-Z-АА | 0.265 м² | 800 мм | 795 мм | 550 мм | 545 мм | скрытые защелки |
| AL-STS-1-800х600-Z-АА | 0.289 м² | 800 мм | 795 мм | 600 мм | 595 мм | скрытые защелки |
| AL-STS-1-800х625-Z-АА | 0.301 м² | 800 мм | 795 мм | 625 мм | 620 мм | скрытые защелки |
| AL-STS-1-800х650-Z-АА | 0.313 м² | 800 мм | 795 мм | 650 мм | 645 мм | скрытые защелки |
| AL-STS-1-825х100-Z-АА | 0.050 м² | 825 мм | 820 мм | 100 мм | 95 мм | скрытые защелки |
| AL-STS-1-825х125-Z-АА | 0.062 м² | 825 мм | 820 мм | 125 мм | 120 мм | скрытые защелки |
| AL-STS-1-825х150-Z-АА | 0.074 м² | 825 мм | 820 мм | 150 мм | 145 мм | скрытые защелки |
| AL-STS-1-825х200-Z-АА | 0.099 м² | 825 мм | 820 мм | 200 мм | 195 мм | скрытые защелки |
| AL-STS-1-825х225-Z-АА | 0.112 м² | 825 мм | 820 мм | 225 мм | 220 мм | скрытые защелки |
| AL-STS-1-825х250-Z-АА | 0.124 м² | 825 мм | 820 мм | 250 мм | 245 мм | скрытые защелки |
| AL-STS-1-825х300-Z-АА | 0.149 м² | 825 мм | 820 мм | 300 мм | 295 мм | скрытые защелки |
| AL-STS-1-825х325-Z-АА | 0.161 м² | 825 мм | 820 мм | 325 мм | 320 мм | скрытые защелки |
| AL-STS-1-825х350-Z-АА | 0.174 м² | 825 мм | 820 мм | 350 мм | 345 мм | скрытые защелки |
| AL-STS-1-825х400-Z-АА | 0.199 м² | 825 мм | 820 мм | 400 мм | 395 мм | скрытые защелки |
| AL-STS-1-825х425-Z-АА | 0.211 м² | 825 мм | 820 мм | 425 мм | 420 мм | скрытые защелки |
| AL-STS-1-825х450-Z-АА | 0.223 м² | 825 мм | 820 мм | 450 мм | 445 мм | скрытые защелки |
| AL-STS-1-825х500-Z-АА | 0.248 м² | 825 мм | 820 мм | 500 мм | 495 мм | скрытые защелки |
| AL-STS-1-825х525-Z-АА | 0.261 м² | 825 мм | 820 мм | 525 мм | 520 мм | скрытые защелки |
| AL-STS-1-825х550-Z-АА | 0.273 м² | 825 мм | 820 мм | 550 мм | 545 мм | скрытые защелки |
| AL-STS-1-825х600-Z-АА | 0.298 м² | 825 мм | 820 мм | 600 мм | 595 мм | скрытые защелки |
| AL-STS-1-825х625-Z-АА | 0.310 м² | 825 мм | 820 мм | 625 мм | 620 мм | скрытые защелки |
| AL-STS-1-825х650-Z-АА | 0.323 м² | 825 мм | 820 мм | 650 мм | 645 мм | скрытые защелки |
| AL-STS-1-850х100-Z-АА | 0.051 м² | 850 мм | 845 мм | 100 мм | 95 мм | скрытые защелки |
| AL-STS-1-850х125-Z-АА | 0.064 м² | 850 мм | 845 мм | 125 мм | 120 мм | скрытые защелки |
| AL-STS-1-850х150-Z-АА | 0.077 м² | 850 мм | 845 мм | 150 мм | 145 мм | скрытые защелки |
| AL-STS-1-850х200-Z-АА | 0.102 м² | 850 мм | 845 мм | 200 мм | 195 мм | скрытые защелки |
| AL-STS-1-850х225-Z-АА | 0.115 м² | 850 мм | 845 мм | 225 мм | 220 мм | скрытые защелки |
| AL-STS-1-850х250-Z-АА | 0.128 м² | 850 мм | 845 мм | 250 мм | 245 мм | скрытые защелки |
| AL-STS-1-850х300-Z-АА | 0.153 м² | 850 мм | 845 мм | 300 мм | 295 мм | скрытые защелки |
| AL-STS-1-850х325-Z-АА | 0.166 м² | 850 мм | 845 мм | 325 мм | 320 мм | скрытые защелки |
| AL-STS-1-850х350-Z-АА | 0.179 м² | 850 мм | 845 мм | 350 мм | 345 мм | скрытые защелки |
| AL-STS-1-850х400-Z-АА | 0.205 м² | 850 мм | 845 мм | 400 мм | 395 мм | скрытые защелки |
| AL-STS-1-850х425-Z-АА | 0.217 м² | 850 мм | 845 мм | 425 мм | 420 мм | скрытые защелки |
| AL-STS-1-850х450-Z-АА | 0.230 м² | 850 мм | 845 мм | 450 мм | 445 мм | скрытые защелки |
| AL-STS-1-850х500-Z-АА | 0.256 м² | 850 мм | 845 мм | 500 мм | 495 мм | скрытые защелки |
| AL-STS-1-850х525-Z-АА | 0.268 м² | 850 мм | 845 мм | 525 мм | 520 мм | скрытые защелки |
| AL-STS-1-850х550-Z-АА | 0.281 м² | 850 мм | 845 мм | 550 мм | 545 мм | скрытые защелки |
| AL-STS-1-850х600-Z-АА | 0.307 м² | 850 мм | 845 мм | 600 мм | 595 мм | скрытые защелки |
| AL-STS-1-850х625-Z-АА | 0.320 м² | 850 мм | 845 мм | 625 мм | 620 мм | скрытые защелки |
| AL-STS-1-850х650-Z-АА | 0.332 м² | 850 мм | 845 мм | 650 мм | 645 мм | скрытые защелки |
| AL-STS-1-900х100-Z-АА | 0.054 м² | 900 мм | 895 мм | 100 мм | 95 мм | скрытые защелки |
| AL-STS-1-900х125-Z-АА | 0.068 м² | 900 мм | 895 мм | 125 мм | 120 мм | скрытые защелки |
| AL-STS-1-900х150-Z-АА | 0.081 м² | 900 мм | 895 мм | 150 мм | 145 мм | скрытые защелки |
| AL-STS-1-900х200-Z-АА | 0.108 м² | 900 мм | 895 мм | 200 мм | 195 мм | скрытые защелки |
| AL-STS-1-900х225-Z-АА | 0.122 м² | 900 мм | 895 мм | 225 мм | 220 мм | скрытые защелки |
| AL-STS-1-900х250-Z-АА | 0.135 м² | 900 мм | 895 мм | 250 мм | 245 мм | скрытые защелки |
| AL-STS-1-900х300-Z-АА | 0.162 м² | 900 мм | 895 мм | 300 мм | 295 мм | скрытые защелки |
| AL-STS-1-900х325-Z-АА | 0.176 м² | 900 мм | 895 мм | 325 мм | 320 мм | скрытые защелки |
| AL-STS-1-900х350-Z-АА | 0.190 м² | 900 мм | 895 мм | 350 мм | 345 мм | скрытые защелки |
| AL-STS-1-900х400-Z-АА | 0.217 м² | 900 мм | 895 мм | 400 мм | 395 мм | скрытые защелки |
| AL-STS-1-900х425-Z-АА | 0.230 м² | 900 мм | 895 мм | 425 мм | 420 мм | скрытые защелки |
| AL-STS-1-900х450-Z-АА | 0.244 м² | 900 мм | 895 мм | 450 мм | 445 мм | скрытые защелки |
| AL-STS-1-900х500-Z-АА | 0.271 м² | 900 мм | 895 мм | 500 мм | 495 мм | скрытые защелки |
| AL-STS-1-900х525-Z-АА | 0.284 м² | 900 мм | 895 мм | 525 мм | 520 мм | скрытые защелки |
| AL-STS-1-900х550-Z-АА | 0.298 м² | 900 мм | 895 мм | 550 мм | 545 мм | скрытые защелки |
| AL-STS-1-900х600-Z-АА | 0.325 м² | 900 мм | 895 мм | 600 мм | 595 мм | скрытые защелки |
| AL-STS-1-900х625-Z-АА | 0.338 м² | 900 мм | 895 мм | 625 мм | 620 мм | скрытые защелки |
| AL-STS-1-900х650-Z-АА | 0.352 м² | 900 мм | 895 мм | 650 мм | 645 мм | скрытые защелки |
| AL-STS-1-925х100-Z-АА | 0.056 м² | 925 мм | 920 мм | 100 мм | 95 мм | скрытые защелки |
| AL-STS-1-925х125-Z-АА | 0.070 м² | 925 мм | 920 мм | 125 мм | 120 мм | скрытые защелки |
| AL-STS-1-925х150-Z-АА | 0.083 м² | 925 мм | 920 мм | 150 мм | 145 мм | скрытые защелки |
| AL-STS-1-925х200-Z-АА | 0.111 м² | 925 мм | 920 мм | 200 мм | 195 мм | скрытые защелки |
| AL-STS-1-925х225-Z-АА | 0.125 м² | 925 мм | 920 мм | 225 мм | 220 мм | скрытые защелки |
| AL-STS-1-925х250-Z-АА | 0.139 м² | 925 мм | 920 мм | 250 мм | 245 мм | скрытые защелки |
| AL-STS-1-925х300-Z-АА | 0.167 м² | 925 мм | 920 мм | 300 мм | 295 мм | скрытые защелки |
| AL-STS-1-925х325-Z-АА | 0.181 м² | 925 мм | 920 мм | 325 мм | 320 мм | скрытые защелки |
| AL-STS-1-925х350-Z-АА | 0.195 м² | 925 мм | 920 мм | 350 мм | 345 мм | скрытые защелки |
| AL-STS-1-925х400-Z-АА | 0.223 м² | 925 мм | 920 мм | 400 мм | 395 мм | скрытые защелки |
| AL-STS-1-925х425-Z-АА | 0.237 м² | 925 мм | 920 мм | 425 мм | 420 мм | скрытые защелки |
| AL-STS-1-925х450-Z-АА | 0.250 м² | 925 мм | 920 мм | 450 мм | 445 мм | скрытые защелки |
| AL-STS-1-925х500-Z-АА | 0.278 м² | 925 мм | 920 мм | 500 мм | 495 мм | скрытые защелки |
| AL-STS-1-925х525-Z-АА | 0.292 м² | 925 мм | 920 мм | 525 мм | 520 мм | скрытые защелки |
| AL-STS-1-925х550-Z-АА | 0.306 м² | 925 мм | 920 мм | 550 мм | 545 мм | скрытые защелки |
| AL-STS-1-925х600-Z-АА | 0.334 м² | 925 мм | 920 мм | 600 мм | 595 мм | скрытые защелки |
| AL-STS-1-925х625-Z-АА | 0.348 м² | 925 мм | 920 мм | 625 мм | 620 мм | скрытые защелки |
| AL-STS-1-925х650-Z-АА | 0.362 м² | 925 мм | 920 мм | 650 мм | 645 мм | скрытые защелки |
| AL-STS-1-950х100-Z-АА | 0.057 м² | 950 мм | 945 мм | 100 мм | 95 мм | скрытые защелки |
| AL-STS-1-950х125-Z-АА | 0.071 м² | 950 мм | 945 мм | 125 мм | 120 мм | скрытые защелки |
| AL-STS-1-950х150-Z-АА | 0.086 м² | 950 мм | 945 мм | 150 мм | 145 мм | скрытые защелки |
| AL-STS-1-950х200-Z-АА | 0.114 м² | 950 мм | 945 мм | 200 мм | 195 мм | скрытые защелки |
| AL-STS-1-950х225-Z-АА | 0.129 м² | 950 мм | 945 мм | 225 мм | 220 мм | скрытые защелки |
| AL-STS-1-950х250-Z-АА | 0.143 м² | 950 мм | 945 мм | 250 мм | 245 мм | скрытые защелки |
| AL-STS-1-950х300-Z-АА | 0.171 м² | 950 мм | 945 мм | 300 мм | 295 мм | скрытые защелки |
| AL-STS-1-950х325-Z-АА | 0.186 м² | 950 мм | 945 мм | 325 мм | 320 мм | скрытые защелки |
| AL-STS-1-950х350-Z-АА | 0.200 м² | 950 мм | 945 мм | 350 мм | 345 мм | скрытые защелки |
| AL-STS-1-950х400-Z-АА | 0.229 м² | 950 мм | 945 мм | 400 мм | 395 мм | скрытые защелки |
| AL-STS-1-950х425-Z-АА | 0.243 м² | 950 мм | 945 мм | 425 мм | 420 мм | скрытые защелки |
| AL-STS-1-950х450-Z-АА | 0.257 м² | 950 мм | 945 мм | 450 мм | 445 мм | скрытые защелки |
| AL-STS-1-950х500-Z-АА | 0.286 м² | 950 мм | 945 мм | 500 мм | 495 мм | скрытые защелки |
| AL-STS-1-950х525-Z-АА | 0.300 м² | 950 мм | 945 мм | 525 мм | 520 мм | скрытые защелки |
| AL-STS-1-950х550-Z-АА | 0.314 м² | 950 мм | 945 мм | 550 мм | 545 мм | скрытые защелки |
| AL-STS-1-950х600-Z-АА | 0.343 м² | 950 мм | 945 мм | 600 мм | 595 мм | скрытые защелки |
| AL-STS-1-950х625-Z-АА | 0.357 м² | 950 мм | 945 мм | 625 мм | 620 мм | скрытые защелки |
| AL-STS-1-950х650-Z-АА | 0.371 м² | 950 мм | 945 мм | 650 мм | 645 мм | скрытые защелки |
| AL-STS-1-1000х100-Z-АА | 0.060 м² | 1000 мм | 995 мм | 100 мм | 95 мм | скрытые защелки |
| AL-STS-1-1000х125-Z-АА | 0.075 м² | 1000 мм | 995 мм | 125 мм | 120 мм | скрытые защелки |
| AL-STS-1-1000х150-Z-АА | 0.090 м² | 1000 мм | 995 мм | 150 мм | 145 мм | скрытые защелки |
| AL-STS-1-1000х200-Z-АА | 0.120 м² | 1000 мм | 995 мм | 200 мм | 195 мм | скрытые защелки |
| AL-STS-1-1000х225-Z-АА | 0.135 м² | 1000 мм | 995 мм | 225 мм | 220 мм | скрытые защелки |
| AL-STS-1-1000х250-Z-АА | 0.150 м² | 1000 мм | 995 мм | 250 мм | 245 мм | скрытые защелки |
| AL-STS-1-1000х300-Z-АА | 0.180 м² | 1000 мм | 995 мм | 300 мм | 295 мм | скрытые защелки |
| AL-STS-1-1000х325-Z-АА | 0.196 м² | 1000 мм | 995 мм | 325 мм | 320 мм | скрытые защелки |
| AL-STS-1-1000х350-Z-АА | 0.211 м² | 1000 мм | 995 мм | 350 мм | 345 мм | скрытые защелки |
| AL-STS-1-1000х400-Z-АА | 0.241 м² | 1000 мм | 995 мм | 400 мм | 395 мм | скрытые защелки |
| AL-STS-1-1000х425-Z-АА | 0.256 м² | 1000 мм | 995 мм | 425 мм | 420 мм | скрытые защелки |
| AL-STS-1-1000х450-Z-АА | 0.271 м² | 1000 мм | 995 мм | 450 мм | 445 мм | скрытые защелки |
| AL-STS-1-1000х500-Z-АА | 0.301 м² | 1000 мм | 995 мм | 500 мм | 495 мм | скрытые защелки |
| AL-STS-1-1000х525-Z-АА | 0.316 м² | 1000 мм | 995 мм | 525 мм | 520 мм | скрытые защелки |
| AL-STS-1-1000х550-Z-АА | 0.331 м² | 1000 мм | 995 мм | 550 мм | 545 мм | скрытые защелки |
| AL-STS-1-1000х600-Z-АА | 0.361 м² | 1000 мм | 995 мм | 600 мм | 595 мм | скрытые защелки |
| AL-STS-1-1000х625-Z-АА | 0.376 м² | 1000 мм | 995 мм | 625 мм | 620 мм | скрытые защелки |
| AL-STS-1-1000х650-Z-АА | 0.391 м² | 1000 мм | 995 мм | 650 мм | 645 мм | скрытые защелки |
| AL-STS-1-1025х100-Z-АА | 0.062 м² | 1025 мм | 1020 мм | 100 мм | 95 мм | скрытые защелки |
| AL-STS-1-1025х125-Z-АА | 0.077 м² | 1025 мм | 1020 мм | 125 мм | 120 мм | скрытые защелки |
| AL-STS-1-1025х150-Z-АА | 0.092 м² | 1025 мм | 1020 мм | 150 мм | 145 мм | скрытые защелки |
| AL-STS-1-1025х200-Z-АА | 0.123 м² | 1025 мм | 1020 мм | 200 мм | 195 мм | скрытые защелки |
| AL-STS-1-1025х225-Z-АА | 0.139 м² | 1025 мм | 1020 мм | 225 мм | 220 мм | скрытые защелки |
| AL-STS-1-1025х250-Z-АА | 0.154 м² | 1025 мм | 1020 мм | 250 мм | 245 мм | скрытые защелки |
| AL-STS-1-1025х300-Z-АА | 0.185 м² | 1025 мм | 1020 мм | 300 мм | 295 мм | скрытые защелки |
| AL-STS-1-1025х325-Z-АА | 0.200 м² | 1025 мм | 1020 мм | 325 мм | 320 мм | скрытые защелки |
| AL-STS-1-1025х350-Z-АА | 0.216 м² | 1025 мм | 1020 мм | 350 мм | 345 мм | скрытые защелки |
| AL-STS-1-1025х400-Z-АА | 0.247 м² | 1025 мм | 1020 мм | 400 мм | 395 мм | скрытые защелки |
| AL-STS-1-1025х425-Z-АА | 0.262 м² | 1025 мм | 1020 мм | 425 мм | 420 мм | скрытые защелки |
| AL-STS-1-1025х450-Z-АА | 0.277 м² | 1025 мм | 1020 мм | 450 мм | 445 мм | скрытые защелки |
| AL-STS-1-1025х500-Z-АА | 0.308 м² | 1025 мм | 1020 мм | 500 мм | 495 мм | скрытые защелки |
| AL-STS-1-1025х525-Z-АА | 0.324 м² | 1025 мм | 1020 мм | 525 мм | 520 мм | скрытые защелки |
| AL-STS-1-1025х550-Z-АА | 0.339 м² | 1025 мм | 1020 мм | 550 мм | 545 мм | скрытые защелки |
| AL-STS-1-1025х600-Z-АА | 0.370 м² | 1025 мм | 1020 мм | 600 мм | 595 мм | скрытые защелки |
| AL-STS-1-1025х625-Z-АА | 0.385 м² | 1025 мм | 1020 мм | 625 мм | 620 мм | скрытые защелки |
| AL-STS-1-1025х650-Z-АА | 0.401 м² | 1025 мм | 1020 мм | 650 мм | 645 мм | скрытые защелки |
| AL-STS-1-1050х100-Z-АА | 0.063 м² | 1050 мм | 1045 мм | 100 мм | 95 мм | скрытые защелки |
| AL-STS-1-1050х125-Z-АА | 0.079 м² | 1050 мм | 1045 мм | 125 мм | 120 мм | скрытые защелки |
| AL-STS-1-1050х150-Z-АА | 0.095 м² | 1050 мм | 1045 мм | 150 мм | 145 мм | скрытые защелки |
| AL-STS-1-1050х200-Z-АА | 0.126 м² | 1050 мм | 1045 мм | 200 мм | 195 мм | скрытые защелки |
| AL-STS-1-1050х225-Z-АА | 0.142 м² | 1050 мм | 1045 мм | 225 мм | 220 мм | скрытые защелки |
| AL-STS-1-1050х250-Z-АА | 0.158 м² | 1050 мм | 1045 мм | 250 мм | 245 мм | скрытые защелки |
| AL-STS-1-1050х300-Z-АА | 0.190 м² | 1050 мм | 1045 мм | 300 мм | 295 мм | скрытые защелки |
| AL-STS-1-1050х325-Z-АА | 0.205 м² | 1050 мм | 1045 мм | 325 мм | 320 мм | скрытые защелки |
| AL-STS-1-1050х350-Z-АА | 0.221 м² | 1050 мм | 1045 мм | 350 мм | 345 мм | скрытые защелки |
| AL-STS-1-1050х400-Z-АА | 0.253 м² | 1050 мм | 1045 мм | 400 мм | 395 мм | скрытые защелки |
| AL-STS-1-1050х425-Z-АА | 0.268 м² | 1050 мм | 1045 мм | 425 мм | 420 мм | скрытые защелки |
| AL-STS-1-1050х450-Z-АА | 0.284 м² | 1050 мм | 1045 мм | 450 мм | 445 мм | скрытые защелки |
| AL-STS-1-1050х500-Z-АА | 0.316 м² | 1050 мм | 1045 мм | 500 мм | 495 мм | скрытые защелки |
| AL-STS-1-1050х525-Z-АА | 0.332 м² | 1050 мм | 1045 мм | 525 мм | 520 мм | скрытые защелки |
| AL-STS-1-1050х550-Z-АА | 0.347 м² | 1050 мм | 1045 мм | 550 мм | 545 мм | скрытые защелки |
| AL-STS-1-1050х600-Z-АА | 0.379 м² | 1050 мм | 1045 мм | 600 мм | 595 мм | скрытые защелки |
| AL-STS-1-1050х625-Z-АА | 0.395 м² | 1050 мм | 1045 мм | 625 мм | 620 мм | скрытые защелки |
| AL-STS-1-1050х650-Z-АА | 0.411 м² | 1050 мм | 1045 мм | 650 мм | 645 мм | скрытые защелки |
| AL-STS-1-1100х100-Z-АА | 0.066 м² | 1100 мм | 1095 мм | 100 мм | 95 мм | скрытые защелки |
| AL-STS-1-1100х125-Z-АА | 0.083 м² | 1100 мм | 1095 мм | 125 мм | 120 мм | скрытые защелки |
| AL-STS-1-1100х150-Z-АА | 0.099 м² | 1100 мм | 1095 мм | 150 мм | 145 мм | скрытые защелки |
| AL-STS-1-1100х200-Z-АА | 0.132 м² | 1100 мм | 1095 мм | 200 мм | 195 мм | скрытые защелки |
| AL-STS-1-1100х225-Z-АА | 0.149 м² | 1100 мм | 1095 мм | 225 мм | 220 мм | скрытые защелки |
| AL-STS-1-1100х250-Z-АА | 0.165 м² | 1100 мм | 1095 мм | 250 мм | 245 мм | скрытые защелки |
| AL-STS-1-1100х300-Z-АА | 0.199 м² | 1100 мм | 1095 мм | 300 мм | 295 мм | скрытые защелки |
| AL-STS-1-1100х325-Z-АА | 0.215 м² | 1100 мм | 1095 мм | 325 мм | 320 мм | скрытые защелки |
| AL-STS-1-1100х350-Z-АА | 0.232 м² | 1100 мм | 1095 мм | 350 мм | 345 мм | скрытые защелки |
| AL-STS-1-1100х400-Z-АА | 0.265 м² | 1100 мм | 1095 мм | 400 мм | 395 мм | скрытые защелки |
| AL-STS-1-1100х425-Z-АА | 0.281 м² | 1100 мм | 1095 мм | 425 мм | 420 мм | скрытые защелки |
| AL-STS-1-1100х450-Z-АА | 0.298 м² | 1100 мм | 1095 мм | 450 мм | 445 мм | скрытые защелки |
| AL-STS-1-1100х500-Z-АА | 0.331 м² | 1100 мм | 1095 мм | 500 мм | 495 мм | скрытые защелки |
| AL-STS-1-1100х525-Z-АА | 0.347 м² | 1100 мм | 1095 мм | 525 мм | 520 мм | скрытые защелки |
| AL-STS-1-1100х550-Z-АА | 0.364 м² | 1100 мм | 1095 мм | 550 мм | 545 мм | скрытые защелки |
| AL-STS-1-1100х600-Z-АА | 0.397 м² | 1100 мм | 1095 мм | 600 мм | 595 мм | скрытые защелки |
| AL-STS-1-1100х625-Z-АА | 0.414 м² | 1100 мм | 1095 мм | 625 мм | 620 мм | скрытые защелки |
| AL-STS-1-1100х650-Z-АА | 0.430 м² | 1100 мм | 1095 мм | 650 мм | 645 мм | скрытые защелки |
| AL-STS-1-1125х100-Z-АА | 0.068 м² | 1125 мм | 1120 мм | 100 мм | 95 мм | скрытые защелки |
| AL-STS-1-1125х125-Z-АА | 0.085 м² | 1125 мм | 1120 мм | 125 мм | 120 мм | скрытые защелки |
| AL-STS-1-1125х150-Z-АА | 0.102 м² | 1125 мм | 1120 мм | 150 мм | 145 мм | скрытые защелки |
| AL-STS-1-1125х200-Z-АА | 0.135 м² | 1125 мм | 1120 мм | 200 мм | 195 мм | скрытые защелки |
| AL-STS-1-1125х225-Z-АА | 0.152 м² | 1125 мм | 1120 мм | 225 мм | 220 мм | скрытые защелки |
| AL-STS-1-1125х250-Z-АА | 0.169 м² | 1125 мм | 1120 мм | 250 мм | 245 мм | скрытые защелки |
| AL-STS-1-1125х300-Z-АА | 0.203 м² | 1125 мм | 1120 мм | 300 мм | 295 мм | скрытые защелки |
| AL-STS-1-1125х325-Z-АА | 0.220 м² | 1125 мм | 1120 мм | 325 мм | 320 мм | скрытые защелки |
| AL-STS-1-1125х350-Z-АА | 0.237 м² | 1125 мм | 1120 мм | 350 мм | 345 мм | скрытые защелки |
| AL-STS-1-1125х400-Z-АА | 0.271 м² | 1125 мм | 1120 мм | 400 мм | 395 мм | скрытые защелки |
| AL-STS-1-1125х425-Z-АА | 0.288 м² | 1125 мм | 1120 мм | 425 мм | 420 мм | скрытые защелки |
| AL-STS-1-1125х450-Z-АА | 0.305 м² | 1125 мм | 1120 мм | 450 мм | 445 мм | скрытые защелки |
| AL-STS-1-1125х500-Z-АА | 0.338 м² | 1125 мм | 1120 мм | 500 мм | 495 мм | скрытые защелки |
| AL-STS-1-1125х525-Z-АА | 0.355 м² | 1125 мм | 1120 мм | 525 мм | 520 мм | скрытые защелки |
| AL-STS-1-1125х550-Z-АА | 0.372 м² | 1125 мм | 1120 мм | 550 мм | 545 мм | скрытые защелки |
| AL-STS-1-1125х600-Z-АА | 0.406 м² | 1125 мм | 1120 мм | 600 мм | 595 мм | скрытые защелки |
| AL-STS-1-1125х625-Z-АА | 0.423 м² | 1125 мм | 1120 мм | 625 мм | 620 мм | скрытые защелки |
| AL-STS-1-1125х650-Z-АА | 0.440 м² | 1125 мм | 1120 мм | 650 мм | 645 мм | скрытые защелки |
| AL-STS-1-1150х100-Z-АА | 0.069 м² | 1150 мм | 1145 мм | 100 мм | 95 мм | скрытые защелки |
| AL-STS-1-1150х125-Z-АА | 0.086 м² | 1150 мм | 1145 мм | 125 мм | 120 мм | скрытые защелки |
| AL-STS-1-1150х150-Z-АА | 0.104 м² | 1150 мм | 1145 мм | 150 мм | 145 мм | скрытые защелки |
| AL-STS-1-1150х200-Z-АА | 0.138 м² | 1150 мм | 1145 мм | 200 мм | 195 мм | скрытые защелки |
| AL-STS-1-1150х225-Z-АА | 0.156 м² | 1150 мм | 1145 мм | 225 мм | 220 мм | скрытые защелки |
| AL-STS-1-1150х250-Z-АА | 0.173 м² | 1150 мм | 1145 мм | 250 мм | 245 мм | скрытые защелки |
| AL-STS-1-1150х300-Z-АА | 0.208 м² | 1150 мм | 1145 мм | 300 мм | 295 мм | скрытые защелки |
| AL-STS-1-1150х325-Z-АА | 0.225 м² | 1150 мм | 1145 мм | 325 мм | 320 мм | скрытые защелки |
| AL-STS-1-1150х350-Z-АА | 0.242 м² | 1150 мм | 1145 мм | 350 мм | 345 мм | скрытые защелки |
| AL-STS-1-1150х400-Z-АА | 0.277 м² | 1150 мм | 1145 мм | 400 мм | 395 мм | скрытые защелки |
| AL-STS-1-1150х425-Z-АА | 0.294 м² | 1150 мм | 1145 мм | 425 мм | 420 мм | скрытые защелки |
| AL-STS-1-1150х450-Z-АА | 0.311 м² | 1150 мм | 1145 мм | 450 мм | 445 мм | скрытые защелки |
| AL-STS-1-1150х500-Z-АА | 0.346 м² | 1150 мм | 1145 мм | 500 мм | 495 мм | скрытые защелки |
| AL-STS-1-1150х525-Z-АА | 0.363 м² | 1150 мм | 1145 мм | 525 мм | 520 мм | скрытые защелки |
| AL-STS-1-1150х550-Z-АА | 0.381 м² | 1150 мм | 1145 мм | 550 мм | 545 мм | скрытые защелки |
| AL-STS-1-1150х600-Z-АА | 0.415 м² | 1150 мм | 1145 мм | 600 мм | 595 мм | скрытые защелки |
| AL-STS-1-1150х625-Z-АА | 0.432 м² | 1150 мм | 1145 мм | 625 мм | 620 мм | скрытые защелки |
| AL-STS-1-1150х650-Z-АА | 0.450 м² | 1150 мм | 1145 мм | 650 мм | 645 мм | скрытые защелки |
| AL-STS-1-1200х100-Z-АА | 0.072 м² | 1200 мм | 1195 мм | 100 мм | 95 мм | скрытые защелки |
| AL-STS-1-1200х125-Z-АА | 0.090 м² | 1200 мм | 1195 мм | 125 мм | 120 мм | скрытые защелки |
| AL-STS-1-1200х150-Z-АА | 0.108 м² | 1200 мм | 1195 мм | 150 мм | 145 мм | скрытые защелки |
| AL-STS-1-1200х200-Z-АА | 0.144 м² | 1200 мм | 1195 мм | 200 мм | 195 мм | скрытые защелки |
| AL-STS-1-1200х225-Z-АА | 0.162 м² | 1200 мм | 1195 мм | 225 мм | 220 мм | скрытые защелки |
| AL-STS-1-1200х250-Z-АА | 0.180 м² | 1200 мм | 1195 мм | 250 мм | 245 мм | скрытые защелки |
| AL-STS-1-1200х300-Z-АА | 0.217 м² | 1200 мм | 1195 мм | 300 мм | 295 мм | скрытые защелки |
| AL-STS-1-1200х325-Z-АА | 0.235 м² | 1200 мм | 1195 мм | 325 мм | 320 мм | скрытые защелки |
| AL-STS-1-1200х350-Z-АА | 0.253 м² | 1200 мм | 1195 мм | 350 мм | 345 мм | скрытые защелки |
| AL-STS-1-1200х400-Z-АА | 0.289 м² | 1200 мм | 1195 мм | 400 мм | 395 мм | скрытые защелки |
| AL-STS-1-1200х425-Z-АА | 0.307 м² | 1200 мм | 1195 мм | 425 мм | 420 мм | скрытые защелки |
| AL-STS-1-1200х450-Z-АА | 0.325 м² | 1200 мм | 1195 мм | 450 мм | 445 мм | скрытые защелки |
| AL-STS-1-1200х500-Z-АА | 0.361 м² | 1200 мм | 1195 мм | 500 мм | 495 мм | скрытые защелки |
| AL-STS-1-1200х525-Z-АА | 0.379 м² | 1200 мм | 1195 мм | 525 мм | 520 мм | скрытые защелки |
| AL-STS-1-1200х550-Z-АА | 0.397 м² | 1200 мм | 1195 мм | 550 мм | 545 мм | скрытые защелки |
| AL-STS-1-1200х600-Z-АА | 0.433 м² | 1200 мм | 1195 мм | 600 мм | 595 мм | скрытые защелки |
| AL-STS-1-1200х625-Z-АА | 0.451 м² | 1200 мм | 1195 мм | 625 мм | 620 мм | скрытые защелки |
| AL-STS-1-1200х650-Z-АА | 0.469 м² | 1200 мм | 1195 мм | 650 мм | 645 мм | скрытые защелки |
| AL-STS-1-1225х100-Z-АА | 0.074 м² | 1225 мм | 1220 мм | 100 мм | 95 мм | скрытые защелки |
| AL-STS-1-1225х125-Z-АА | 0.092 м² | 1225 мм | 1220 мм | 125 мм | 120 мм | скрытые защелки |
| AL-STS-1-1225х150-Z-АА | 0.111 м² | 1225 мм | 1220 мм | 150 мм | 145 мм | скрытые защелки |
| AL-STS-1-1225х200-Z-АА | 0.147 м² | 1225 мм | 1220 мм | 200 мм | 195 мм | скрытые защелки |
| AL-STS-1-1225х225-Z-АА | 0.166 м² | 1225 мм | 1220 мм | 225 мм | 220 мм | скрытые защелки |
| AL-STS-1-1225х250-Z-АА | 0.184 м² | 1225 мм | 1220 мм | 250 мм | 245 мм | скрытые защелки |
| AL-STS-1-1225х300-Z-АА | 0.221 м² | 1225 мм | 1220 мм | 300 мм | 295 мм | скрытые защелки |
| AL-STS-1-1225х325-Z-АА | 0.240 м² | 1225 мм | 1220 мм | 325 мм | 320 мм | скрытые защелки |
| AL-STS-1-1225х350-Z-АА | 0.258 м² | 1225 мм | 1220 мм | 350 мм | 345 мм | скрытые защелки |
| AL-STS-1-1225х400-Z-АА | 0.295 м² | 1225 мм | 1220 мм | 400 мм | 395 мм | скрытые защелки |
| AL-STS-1-1225х425-Z-АА | 0.313 м² | 1225 мм | 1220 мм | 425 мм | 420 мм | скрытые защелки |
| AL-STS-1-1225х450-Z-АА | 0.332 м² | 1225 мм | 1220 мм | 450 мм | 445 мм | скрытые защелки |
| AL-STS-1-1225х500-Z-АА | 0.368 м² | 1225 мм | 1220 мм | 500 мм | 495 мм | скрытые защелки |
| AL-STS-1-1225х525-Z-АА | 0.387 м² | 1225 мм | 1220 мм | 525 мм | 520 мм | скрытые защелки |
| AL-STS-1-1225х550-Z-АА | 0.405 м² | 1225 мм | 1220 мм | 550 мм | 545 мм | скрытые защелки |
| AL-STS-1-1225х600-Z-АА | 0.442 м² | 1225 мм | 1220 мм | 600 мм | 595 мм | скрытые защелки |
| AL-STS-1-1225х625-Z-АА | 0.461 м² | 1225 мм | 1220 мм | 625 мм | 620 мм | скрытые защелки |
| AL-STS-1-1225х650-Z-АА | 0.479 м² | 1225 мм | 1220 мм | 650 мм | 645 мм | скрытые защелки |
| AL-STS-1-1250х100-Z-АА | 0.075 м² | 1250 мм | 1245 мм | 100 мм | 95 мм | скрытые защелки |
| AL-STS-1-1250х125-Z-АА | 0.094 м² | 1250 мм | 1245 мм | 125 мм | 120 мм | скрытые защелки |
| AL-STS-1-1250х150-Z-АА | 0.113 м² | 1250 мм | 1245 мм | 150 мм | 145 мм | скрытые защелки |
| AL-STS-1-1250х200-Z-АА | 0.150 м² | 1250 мм | 1245 мм | 200 мм | 195 мм | скрытые защелки |
| AL-STS-1-1250х225-Z-АА | 0.169 м² | 1250 мм | 1245 мм | 225 мм | 220 мм | скрытые защелки |
| AL-STS-1-1250х250-Z-АА | 0.188 м² | 1250 мм | 1245 мм | 250 мм | 245 мм | скрытые защелки |
| AL-STS-1-1250х300-Z-АА | 0.226 м² | 1250 мм | 1245 мм | 300 мм | 295 мм | скрытые защелки |
| AL-STS-1-1250х325-Z-АА | 0.244 м² | 1250 мм | 1245 мм | 325 мм | 320 мм | скрытые защелки |
| AL-STS-1-1250х350-Z-АА | 0.263 м² | 1250 мм | 1245 мм | 350 мм | 345 мм | скрытые защелки |
| AL-STS-1-1250х400-Z-АА | 0.301 м² | 1250 мм | 1245 мм | 400 мм | 395 мм | скрытые защелки |
| AL-STS-1-1250х425-Z-АА | 0.320 м² | 1250 мм | 1245 мм | 425 мм | 420 мм | скрытые защелки |
| AL-STS-1-1250х450-Z-АА | 0.338 м² | 1250 мм | 1245 мм | 450 мм | 445 мм | скрытые защелки |
| AL-STS-1-1250х500-Z-АА | 0.376 м² | 1250 мм | 1245 мм | 500 мм | 495 мм | скрытые защелки |
| AL-STS-1-1250х525-Z-АА | 0.395 м² | 1250 мм | 1245 мм | 525 мм | 520 мм | скрытые защелки |
| AL-STS-1-1250х550-Z-АА | 0.414 м² | 1250 мм | 1245 мм | 550 мм | 545 мм | скрытые защелки |
| AL-STS-1-1250х600-Z-АА | 0.451 м² | 1250 мм | 1245 мм | 600 мм | 595 мм | скрытые защелки |
| AL-STS-1-1250х625-Z-АА | 0.470 м² | 1250 мм | 1245 мм | 625 мм | 620 мм | скрытые защелки |
| AL-STS-1-1250х650-Z-АА | 0.489 м² | 1250 мм | 1245 мм | 650 мм | 645 мм | скрытые защелки |
| AL-STS-1-1300х100-Z-АА | 0.078 м² | 1300 мм | 1295 мм | 100 мм | 95 мм | скрытые защелки |
| AL-STS-1-1300х125-Z-АА | 0.098 м² | 1300 мм | 1295 мм | 125 мм | 120 мм | скрытые защелки |
| AL-STS-1-1300х150-Z-АА | 0.117 м² | 1300 мм | 1295 мм | 150 мм | 145 мм | скрытые защелки |
| AL-STS-1-1300х200-Z-АА | 0.156 м² | 1300 мм | 1295 мм | 200 мм | 195 мм | скрытые защелки |
| AL-STS-1-1300х225-Z-АА | 0.176 м² | 1300 мм | 1295 мм | 225 мм | 220 мм | скрытые защелки |
| AL-STS-1-1300х250-Z-АА | 0.196 м² | 1300 мм | 1295 мм | 250 мм | 245 мм | скрытые защелки |
| AL-STS-1-1300х300-Z-АА | 0.235 м² | 1300 мм | 1295 мм | 300 мм | 295 мм | скрытые защелки |
| AL-STS-1-1300х325-Z-АА | 0.254 м² | 1300 мм | 1295 мм | 325 мм | 320 мм | скрытые защелки |
| AL-STS-1-1300х350-Z-АА | 0.274 м² | 1300 мм | 1295 мм | 350 мм | 345 мм | скрытые защелки |
| AL-STS-1-1300х400-Z-АА | 0.313 м² | 1300 мм | 1295 мм | 400 мм | 395 мм | скрытые защелки |
| AL-STS-1-1300х425-Z-АА | 0.332 м² | 1300 мм | 1295 мм | 425 мм | 420 мм | скрытые защелки |
| AL-STS-1-1300х450-Z-АА | 0.352 м² | 1300 мм | 1295 мм | 450 мм | 445 мм | скрытые защелки |
| AL-STS-1-1300х500-Z-АА | 0.391 м² | 1300 мм | 1295 мм | 500 мм | 495 мм | скрытые защелки |
| AL-STS-1-1300х525-Z-АА | 0.411 м² | 1300 мм | 1295 мм | 525 мм | 520 мм | скрытые защелки |
| AL-STS-1-1300х550-Z-АА | 0.430 м² | 1300 мм | 1295 мм | 550 мм | 545 мм | скрытые защелки |
| AL-STS-1-1300х600-Z-АА | 0.469 м² | 1300 мм | 1295 мм | 600 мм | 595 мм | скрытые защелки |
| AL-STS-1-1300х625-Z-АА | 0.489 м² | 1300 мм | 1295 мм | 625 мм | 620 мм | скрытые защелки |
| AL-STS-1-1300х650-Z-АА | 0.508 м² | 1300 мм | 1295 мм | 650 мм | 645 мм | скрытые защелки |
| AL-STS-1-1325х100-Z-АА | 0.080 м² | 1325 мм | 1320 мм | 100 мм | 95 мм | скрытые защелки |
| AL-STS-1-1325х125-Z-АА | 0.100 м² | 1325 мм | 1320 мм | 125 мм | 120 мм | скрытые защелки |
| AL-STS-1-1325х150-Z-АА | 0.120 м² | 1325 мм | 1320 мм | 150 мм | 145 мм | скрытые защелки |
| AL-STS-1-1325х200-Z-АА | 0.159 м² | 1325 мм | 1320 мм | 200 мм | 195 мм | скрытые защелки |
| AL-STS-1-1325х225-Z-АА | 0.179 м² | 1325 мм | 1320 мм | 225 мм | 220 мм | скрытые защелки |
| AL-STS-1-1325х250-Z-АА | 0.199 м² | 1325 мм | 1320 мм | 250 мм | 245 мм | скрытые защелки |
| AL-STS-1-1325х300-Z-АА | 0.239 м² | 1325 мм | 1320 мм | 300 мм | 295 мм | скрытые защелки |
| AL-STS-1-1325х325-Z-АА | 0.259 м² | 1325 мм | 1320 мм | 325 мм | 320 мм | скрытые защелки |
| AL-STS-1-1325х350-Z-АА | 0.279 м² | 1325 мм | 1320 мм | 350 мм | 345 мм | скрытые защелки |
| AL-STS-1-1325х400-Z-АА | 0.319 м² | 1325 мм | 1320 мм | 400 мм | 395 мм | скрытые защелки |
| AL-STS-1-1325х425-Z-АА | 0.339 м² | 1325 мм | 1320 мм | 425 мм | 420 мм | скрытые защелки |
| AL-STS-1-1325х450-Z-АА | 0.359 м² | 1325 мм | 1320 мм | 450 мм | 445 мм | скрытые защелки |
| AL-STS-1-1325х500-Z-АА | 0.399 м² | 1325 мм | 1320 мм | 500 мм | 495 мм | скрытые защелки |
| AL-STS-1-1325х525-Z-АА | 0.418 м² | 1325 мм | 1320 мм | 525 мм | 520 мм | скрытые защелки |
| AL-STS-1-1325х550-Z-АА | 0.438 м² | 1325 мм | 1320 мм | 550 мм | 545 мм | скрытые защелки |
| AL-STS-1-1325х600-Z-АА | 0.478 м² | 1325 мм | 1320 мм | 600 мм | 595 мм | скрытые защелки |
| AL-STS-1-1325х625-Z-АА | 0.498 м² | 1325 мм | 1320 мм | 625 мм | 620 мм | скрытые защелки |
| AL-STS-1-1325х650-Z-АА | 0.518 м² | 1325 мм | 1320 мм | 650 мм | 645 мм | скрытые защелки |
| AL-STS-1-1350х100-Z-АА | 0.081 м² | 1350 мм | 1345 мм | 100 мм | 95 мм | скрытые защелки |
| AL-STS-1-1350х125-Z-АА | 0.102 м² | 1350 мм | 1345 мм | 125 мм | 120 мм | скрытые защелки |
| AL-STS-1-1350х150-Z-АА | 0.122 м² | 1350 мм | 1345 мм | 150 мм | 145 мм | скрытые защелки |
| AL-STS-1-1350х200-Z-АА | 0.162 м² | 1350 мм | 1345 мм | 200 мм | 195 мм | скрытые защелки |
| AL-STS-1-1350х225-Z-АА | 0.183 м² | 1350 мм | 1345 мм | 225 мм | 220 мм | скрытые защелки |
| AL-STS-1-1350х250-Z-АА | 0.203 м² | 1350 мм | 1345 мм | 250 мм | 245 мм | скрытые защелки |
| AL-STS-1-1350х300-Z-АА | 0.244 м² | 1350 мм | 1345 мм | 300 мм | 295 мм | скрытые защелки |
| AL-STS-1-1350х325-Z-АА | 0.264 м² | 1350 мм | 1345 мм | 325 мм | 320 мм | скрытые защелки |
| AL-STS-1-1350х350-Z-АА | 0.284 м² | 1350 мм | 1345 мм | 350 мм | 345 мм | скрытые защелки |
| AL-STS-1-1350х400-Z-АА | 0.325 м² | 1350 мм | 1345 мм | 400 мм | 395 мм | скрытые защелки |
| AL-STS-1-1350х425-Z-АА | 0.345 м² | 1350 мм | 1345 мм | 425 мм | 420 мм | скрытые защелки |
| AL-STS-1-1350х450-Z-АА | 0.365 м² | 1350 мм | 1345 мм | 450 мм | 445 мм | скрытые защелки |
| AL-STS-1-1350х500-Z-АА | 0.406 м² | 1350 мм | 1345 мм | 500 мм | 495 мм | скрытые защелки |
| AL-STS-1-1350х525-Z-АА | 0.426 м² | 1350 мм | 1345 мм | 525 мм | 520 мм | скрытые защелки |
| AL-STS-1-1350х550-Z-АА | 0.447 м² | 1350 мм | 1345 мм | 550 мм | 545 мм | скрытые защелки |
| AL-STS-1-1350х600-Z-АА | 0.487 м² | 1350 мм | 1345 мм | 600 мм | 595 мм | скрытые защелки |
| AL-STS-1-1350х625-Z-АА | 0.508 м² | 1350 мм | 1345 мм | 625 мм | 620 мм | скрытые защелки |
| AL-STS-1-1350х650-Z-АА | 0.528 м² | 1350 мм | 1345 мм | 650 мм | 645 мм | скрытые защелки |
| AL-STS-1-1400х100-Z-АА | 0.084 м² | 1400 мм | 1395 мм | 100 мм | 95 мм | скрытые защелки |
| AL-STS-1-1400х125-Z-АА | 0.105 м² | 1400 мм | 1395 мм | 125 мм | 120 мм | скрытые защелки |
| AL-STS-1-1400х150-Z-АА | 0.126 м² | 1400 мм | 1395 мм | 150 мм | 145 мм | скрытые защелки |
| AL-STS-1-1400х200-Z-АА | 0.168 м² | 1400 мм | 1395 мм | 200 мм | 195 мм | скрытые защелки |
| AL-STS-1-1400х225-Z-АА | 0.190 м² | 1400 мм | 1395 мм | 225 мм | 220 мм | скрытые защелки |
| AL-STS-1-1400х250-Z-АА | 0.211 м² | 1400 мм | 1395 мм | 250 мм | 245 мм | скрытые защелки |
| AL-STS-1-1400х300-Z-АА | 0.253 м² | 1400 мм | 1395 мм | 300 мм | 295 мм | скрытые защелки |
| AL-STS-1-1400х325-Z-АА | 0.274 м² | 1400 мм | 1395 мм | 325 мм | 320 мм | скрытые защелки |
| AL-STS-1-1400х350-Z-АА | 0.295 м² | 1400 мм | 1395 мм | 350 мм | 345 мм | скрытые защелки |
| AL-STS-1-1400х400-Z-АА | 0.337 м² | 1400 мм | 1395 мм | 400 мм | 395 мм | скрытые защелки |
| AL-STS-1-1400х425-Z-АА | 0.358 м² | 1400 мм | 1395 мм | 425 мм | 420 мм | скрытые защелки |
| AL-STS-1-1400х450-Z-АА | 0.379 м² | 1400 мм | 1395 мм | 450 мм | 445 мм | скрытые защелки |
| AL-STS-1-1400х500-Z-АА | 0.421 м² | 1400 мм | 1395 мм | 500 мм | 495 мм | скрытые защелки |
| AL-STS-1-1400х525-Z-АА | 0.442 м² | 1400 мм | 1395 мм | 525 мм | 520 мм | скрытые защелки |
| AL-STS-1-1400х550-Z-АА | 0.463 м² | 1400 мм | 1395 мм | 550 мм | 545 мм | скрытые защелки |
| AL-STS-1-1400х600-Z-АА | 0.505 м² | 1400 мм | 1395 мм | 600 мм | 595 мм | скрытые защелки |
| AL-STS-1-1400х625-Z-АА | 0.526 м² | 1400 мм | 1395 мм | 625 мм | 620 мм | скрытые защелки |
| AL-STS-1-1400х650-Z-АА | 0.547 м² | 1400 мм | 1395 мм | 650 мм | 645 мм | скрытые защелки |
| AL-STS-1-1425х100-Z-АА | 0.086 м² | 1425 мм | 1420 мм | 100 мм | 95 мм | скрытые защелки |
| AL-STS-1-1425х125-Z-АА | 0.107 м² | 1425 мм | 1420 мм | 125 мм | 120 мм | скрытые защелки |
| AL-STS-1-1425х150-Z-АА | 0.129 м² | 1425 мм | 1420 мм | 150 мм | 145 мм | скрытые защелки |
| AL-STS-1-1425х200-Z-АА | 0.171 м² | 1425 мм | 1420 мм | 200 мм | 195 мм | скрытые защелки |
| AL-STS-1-1425х225-Z-АА | 0.193 м² | 1425 мм | 1420 мм | 225 мм | 220 мм | скрытые защелки |
| AL-STS-1-1425х250-Z-АА | 0.214 м² | 1425 мм | 1420 мм | 250 мм | 245 мм | скрытые защелки |
| AL-STS-1-1425х300-Z-АА | 0.257 м² | 1425 мм | 1420 мм | 300 мм | 295 мм | скрытые защелки |
| AL-STS-1-1425х325-Z-АА | 0.279 м² | 1425 мм | 1420 мм | 325 мм | 320 мм | скрытые защелки |
| AL-STS-1-1425х350-Z-АА | 0.300 м² | 1425 мм | 1420 мм | 350 мм | 345 мм | скрытые защелки |
| AL-STS-1-1425х400-Z-АА | 0.343 м² | 1425 мм | 1420 мм | 400 мм | 395 мм | скрытые защелки |
| AL-STS-1-1425х425-Z-АА | 0.364 м² | 1425 мм | 1420 мм | 425 мм | 420 мм | скрытые защелки |
| AL-STS-1-1425х450-Z-АА | 0.386 м² | 1425 мм | 1420 мм | 450 мм | 445 мм | скрытые защелки |
| AL-STS-1-1425х500-Z-АА | 0.429 м² | 1425 мм | 1420 мм | 500 мм | 495 мм | скрытые защелки |
| AL-STS-1-1425х525-Z-АА | 0.450 м² | 1425 мм | 1420 мм | 525 мм | 520 мм | скрытые защелки |
| AL-STS-1-1425х550-Z-АА | 0.472 м² | 1425 мм | 1420 мм | 550 мм | 545 мм | скрытые защелки |
| AL-STS-1-1425х600-Z-АА | 0.514 м² | 1425 мм | 1420 мм | 600 мм | 595 мм | скрытые защелки |
| AL-STS-1-1425х625-Z-АА | 0.536 м² | 1425 мм | 1420 мм | 625 мм | 620 мм | скрытые защелки |
| AL-STS-1-1425х650-Z-АА | 0.557 м² | 1425 мм | 1420 мм | 650 мм | 645 мм | скрытые защелки |
| AL-STS-1-1450х100-Z-АА | 0.087 м² | 1450 мм | 1445 мм | 100 мм | 95 мм | скрытые защелки |
| AL-STS-1-1450х125-Z-АА | 0.109 м² | 1450 мм | 1445 мм | 125 мм | 120 мм | скрытые защелки |
| AL-STS-1-1450х150-Z-АА | 0.131 м² | 1450 мм | 1445 мм | 150 мм | 145 мм | скрытые защелки |
| AL-STS-1-1450х200-Z-АА | 0.174 м² | 1450 мм | 1445 мм | 200 мм | 195 мм | скрытые защелки |
| AL-STS-1-1450х225-Z-АА | 0.196 м² | 1450 мм | 1445 мм | 225 мм | 220 мм | скрытые защелки |
| AL-STS-1-1450х250-Z-АА | 0.218 м² | 1450 мм | 1445 мм | 250 мм | 245 мм | скрытые защелки |
| AL-STS-1-1450х300-Z-АА | 0.262 м² | 1450 мм | 1445 мм | 300 мм | 295 мм | скрытые защелки |
| AL-STS-1-1450х325-Z-АА | 0.284 м² | 1450 мм | 1445 мм | 325 мм | 320 мм | скрытые защелки |
| AL-STS-1-1450х350-Z-АА | 0.305 м² | 1450 мм | 1445 мм | 350 мм | 345 мм | скрытые защелки |
| AL-STS-1-1450х400-Z-АА | 0.349 м² | 1450 мм | 1445 мм | 400 мм | 395 мм | скрытые защелки |
| AL-STS-1-1450х425-Z-АА | 0.371 м² | 1450 мм | 1445 мм | 425 мм | 420 мм | скрытые защелки |
| AL-STS-1-1450х450-Z-АА | 0.393 м² | 1450 мм | 1445 мм | 450 мм | 445 мм | скрытые защелки |
| AL-STS-1-1450х500-Z-АА | 0.436 м² | 1450 мм | 1445 мм | 500 мм | 495 мм | скрытые защелки |
| AL-STS-1-1450х525-Z-АА | 0.458 м² | 1450 мм | 1445 мм | 525 мм | 520 мм | скрытые защелки |
| AL-STS-1-1450х550-Z-АА | 0.480 м² | 1450 мм | 1445 мм | 550 мм | 545 мм | скрытые защелки |
| AL-STS-1-1450х600-Z-АА | 0.523 м² | 1450 мм | 1445 мм | 600 мм | 595 мм | скрытые защелки |
| AL-STS-1-1450х625-Z-АА | 0.545 м² | 1450 мм | 1445 мм | 625 мм | 620 мм | скрытые защелки |
| AL-STS-1-1450х650-Z-АА | 0.567 м² | 1450 мм | 1445 мм | 650 мм | 645 мм | скрытые защелки |
| AL-STS-1-1500х100-Z-АА | 0.090 м² | 1500 мм | 1495 мм | 100 мм | 95 мм | скрытые защелки |
| AL-STS-1-1500х125-Z-АА | 0.113 м² | 1500 мм | 1495 мм | 125 мм | 120 мм | скрытые защелки |
| AL-STS-1-1500х150-Z-АА | 0.135 м² | 1500 мм | 1495 мм | 150 мм | 145 мм | скрытые защелки |
| AL-STS-1-1500х200-Z-АА | 0.180 м² | 1500 мм | 1495 мм | 200 мм | 195 мм | скрытые защелки |
| AL-STS-1-1500х225-Z-АА | 0.203 м² | 1500 мм | 1495 мм | 225 мм | 220 мм | скрытые защелки |
| AL-STS-1-1500х250-Z-АА | 0.226 м² | 1500 мм | 1495 мм | 250 мм | 245 мм | скрытые защелки |
| AL-STS-1-1500х300-Z-АА | 0.271 м² | 1500 мм | 1495 мм | 300 мм | 295 мм | скрытые защелки |
| AL-STS-1-1500х325-Z-АА | 0.293 м² | 1500 мм | 1495 мм | 325 мм | 320 мм | скрытые защелки |
| AL-STS-1-1500х350-Z-АА | 0.316 м² | 1500 мм | 1495 мм | 350 мм | 345 мм | скрытые защелки |
| AL-STS-1-1500х400-Z-АА | 0.361 м² | 1500 мм | 1495 мм | 400 мм | 395 мм | скрытые защелки |
| AL-STS-1-1500х425-Z-АА | 0.384 м² | 1500 мм | 1495 мм | 425 мм | 420 мм | скрытые защелки |
| AL-STS-1-1500х450-Z-АА | 0.406 м² | 1500 мм | 1495 мм | 450 мм | 445 мм | скрытые защелки |
| AL-STS-1-1500х500-Z-АА | 0.451 м² | 1500 мм | 1495 мм | 500 мм | 495 мм | скрытые защелки |
| AL-STS-1-1500х525-Z-АА | 0.474 м² | 1500 мм | 1495 мм | 525 мм | 520 мм | скрытые защелки |
| AL-STS-1-1500х550-Z-АА | 0.496 м² | 1500 мм | 1495 мм | 550 мм | 545 мм | скрытые защелки |
| AL-STS-1-1500х600-Z-АА | 0.541 м² | 1500 мм | 1495 мм | 600 мм | 595 мм | скрытые защелки |
| AL-STS-1-1500х625-Z-АА | 0.564 м² | 1500 мм | 1495 мм | 625 мм | 620 мм | скрытые защелки |
| AL-STS-1-1500х650-Z-АА | 0.587 м² | 1500 мм | 1495 мм | 650 мм | 645 мм | скрытые защелки |

note: column(s) folded — value = type name in every type: Комментарии к типоразмеру
